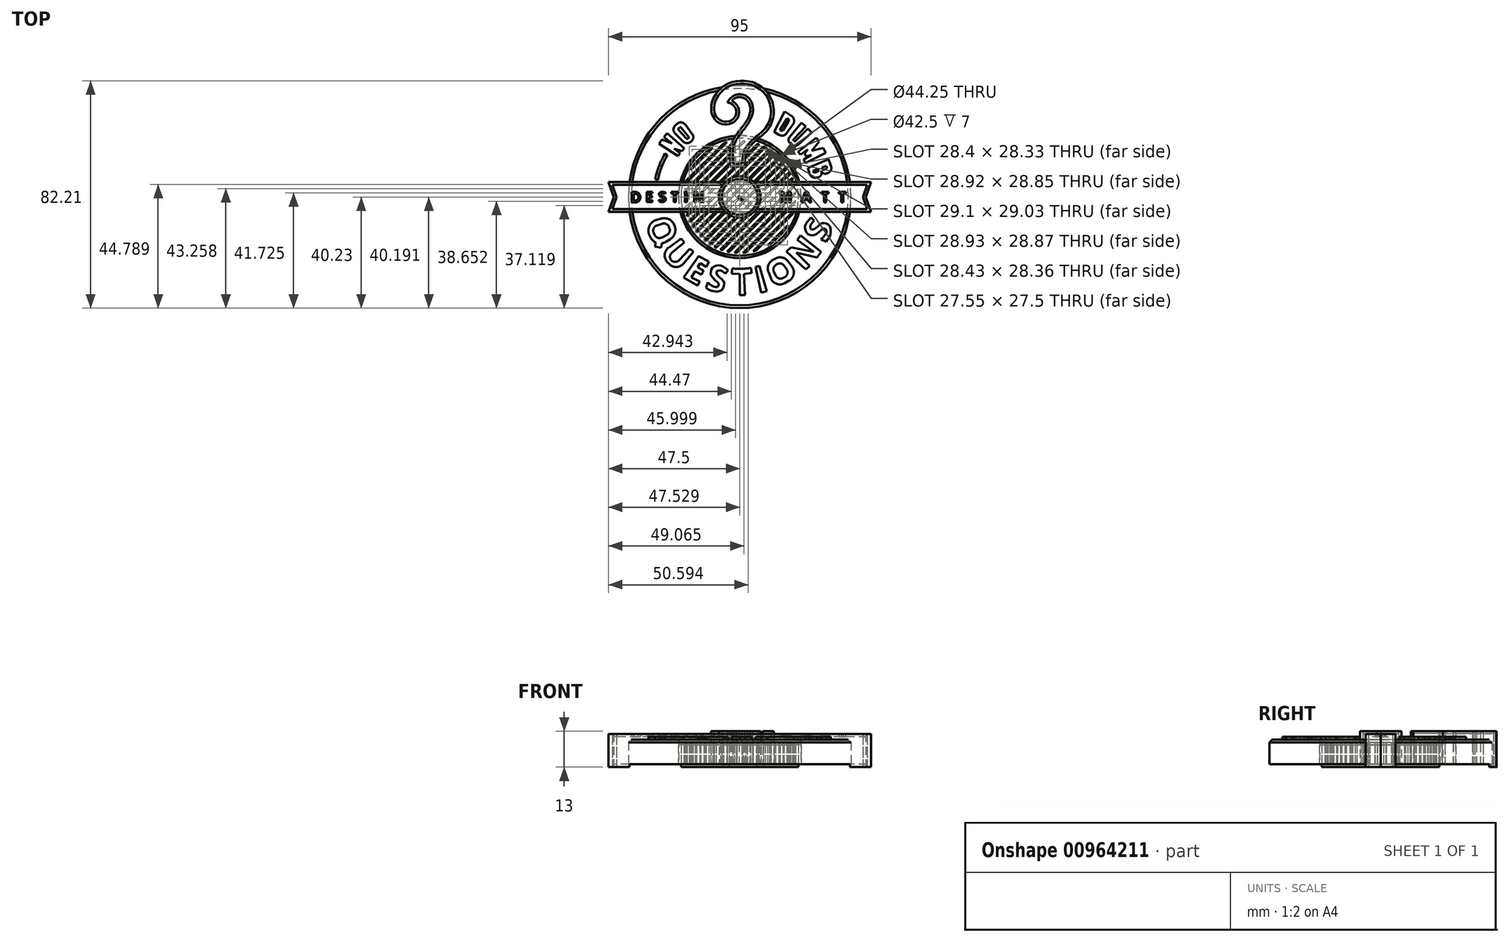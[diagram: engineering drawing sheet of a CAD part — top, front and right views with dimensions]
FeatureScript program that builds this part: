
annotation { "Feature Type Name" : "Feature", "Feature Type Description" : "" }
export const myFeature = defineFeature(function(context is Context, id is Id, definition is map)
    precondition{}
    {
        {
            var Q0;
            Q0=qCreatedBy(makeId("Top.planeOp"),FACE);
            cPlane(context, id + "F0", {"entities" : qUnion([Q0]), "cplaneType" : CPlaneType.OFFSET, "offset" : 11 * mm, "width" : 150 * mm, "height" : 150 * mm});
        }
        {
            var Q0;
            Q0=qCreatedBy(makeId("Top.planeOp"),FACE);
            var sketch = newSketch(context, id + "F1", { "sketchPlane" : qUnion([Q0])});
            skCircle(sketch, "E0", {"center": v(0, 0) * mm, "radius": 22.12 * mm});
            skCircle(sketch, "E1", {"center": v(0, 0) * mm, "radius": 40.23 * mm});
            skSolve(sketch);
        }
        {
            var Q0;
            Q0=qCreatedBy(makeId("Top.planeOp"),FACE);
            var sketch = newSketch(context, id + "F2", { "sketchPlane" : qUnion([Q0])});
            skCircle(sketch, "E2", {"center": v(0, 0) * mm, "radius": 22.25 * mm});
            skCircle(sketch, "E3.0", {"center": v(0, 0) * mm, "radius": 21.25 * mm});
            skCircle(sketch, "E4.0", {"center": v(0, 0) * mm, "radius": 20.25 * mm});
            skLineSegment(sketch, "E5", {"start": v(-14.52, -14.12) * mm, "end": v(14.16, 14.48) * mm});
            skLineSegment(sketch, "E6", {"start": v(-14.08, -14.55) * mm, "end": v(14.58, 14.05) * mm});
            skLineSegment(sketch, "E7.0.1.0", {"start": v(-15.97, -12.45) * mm, "end": v(12.5, 15.93) * mm});
            skLineSegment(sketch, "E7.0.2.0", {"start": v(-17.24, -10.62) * mm, "end": v(10.67, 17.21) * mm});
            skLineSegment(sketch, "E7.0.2.1", {"start": v(-16.9, -11.15) * mm, "end": v(11.18, 16.88) * mm});
            skLineSegment(sketch, "E7.1.7.0", {"start": v(-9.13, -18.07) * mm, "end": v(18.1, 9.08) * mm});
            skLineSegment(sketch, "E7.1.7.1", {"start": v(-8.54, -18.36) * mm, "end": v(18.37, 8.51) * mm});
            skLineSegment(sketch, "E7.1.8.0", {"start": v(-11.1, -16.93) * mm, "end": v(16.97, 11.05) * mm});
            skLineSegment(sketch, "E7.1.8.1", {"start": v(-10.57, -17.27) * mm, "end": v(17.3, 10.54) * mm});
            skLineSegment(sketch, "E7.1.9.0", {"start": v(-12.9, -15.61) * mm, "end": v(15.65, 12.85) * mm});
            skLineSegment(sketch, "E7.1.9.1", {"start": v(-12.4, -16) * mm, "end": v(16.02, 12.38) * mm});
            skLineSegment(sketch, "E8.trimOffspring", {"start": v(12.76, -15.72) * mm, "end": v(15.7, -12.8) * mm});
            skLineSegment(sketch, "E9.trimOffspring", {"start": v(10.02, -17.6) * mm, "end": v(17.57, -10.07) * mm});
            skLineSegment(sketch, "E10.trimOffspring", {"start": v(6.04, -19.33) * mm, "end": v(19.32, -6.07) * mm});
            skLineSegment(sketch, "E11.trimOffspring", {"start": v(4.83, -19.67) * mm, "end": v(19.65, -4.89) * mm});
            skLineSegment(sketch, "E12.trimOffspring", {"start": v(2.11, -20.14) * mm, "end": v(20.14, -2.15) * mm});
            skLineSegment(sketch, "E13.trimOffspring", {"start": v(1.16, -20.22) * mm, "end": v(20.21, -1.22) * mm});
            skLineSegment(sketch, "E14.trimOffspring", {"start": v(-1.9, -20.16) * mm, "end": v(20.17, 1.84) * mm});
            skLineSegment(sketch, "E15.trimOffspring", {"start": v(-1.08, -20.22) * mm, "end": v(20.22, 1.05) * mm});
            skLineSegment(sketch, "E16.trimOffspring", {"start": v(-3.85, -19.88) * mm, "end": v(19.89, 3.82) * mm});
            skLineSegment(sketch, "E17.trimOffspring", {"start": v(-4.58, -19.73) * mm, "end": v(19.74, 4.52) * mm});
            skLineSegment(sketch, "E18.trimOffspring", {"start": v(-6.32, -19.24) * mm, "end": v(19.25, 6.3) * mm});
            skLineSegment(sketch, "E19.trimOffspring", {"start": v(-6.98, -19.01) * mm, "end": v(19.03, 6.92) * mm});
            skLineSegment(sketch, "E20.trimOffspring", {"start": v(-15.58, -12.94) * mm, "end": v(12.97, 15.55) * mm});
            skLineSegment(sketch, "E21.trimOffspring", {"start": v(-18.05, -9.19) * mm, "end": v(9.22, 18.03) * mm});
            skLineSegment(sketch, "E22.trimOffspring", {"start": v(-18.33, -8.6) * mm, "end": v(8.66, 18.3) * mm});
            skLineSegment(sketch, "E23.trimOffspring", {"start": v(-19, -7.03) * mm, "end": v(7.06, 18.98) * mm});
            skLineSegment(sketch, "E24.trimOffspring", {"start": v(-19.22, -6.38) * mm, "end": v(6.44, 19.2) * mm});
            skLineSegment(sketch, "E25.trimOffspring", {"start": v(-19.71, -4.63) * mm, "end": v(4.7, 19.7) * mm});
            skLineSegment(sketch, "E26.trimOffspring", {"start": v(-19.87, -3.92) * mm, "end": v(3.98, 19.86) * mm});
            skLineSegment(sketch, "E27.trimOffspring", {"start": v(-20.15, -1.97) * mm, "end": v(2, 20.15) * mm});
            skLineSegment(sketch, "E28.trimOffspring", {"start": v(-20.22, -1.16) * mm, "end": v(1.22, 20.21) * mm});
            skLineSegment(sketch, "E29.trimOffspring", {"start": v(-20.22, 1.07) * mm, "end": v(-1.04, 20.22) * mm});
            skLineSegment(sketch, "E30.trimOffspring", {"start": v(-20.15, 2.01) * mm, "end": v(-1.95, 20.16) * mm});
            skLineSegment(sketch, "E31.trimOffspring", {"start": v(-19.7, 4.7) * mm, "end": v(-4.67, 19.7) * mm});
            skLineSegment(sketch, "E32.trimOffspring", {"start": v(-19.37, 5.9) * mm, "end": v(-5.83, 19.4) * mm});
            skLineSegment(sketch, "E33.trimOffspring", {"start": v(-17.74, 9.76) * mm, "end": v(-9.73, 17.76) * mm});
            skLineSegment(sketch, "E34.trimOffspring", {"start": v(-16.17, 12.2) * mm, "end": v(-12.15, 16.2) * mm});
            skSolve(sketch);
        }
        {
            var Q0;
            Q0=qCreatedBy(makeId("Top.planeOp"),FACE);
            var sketch = newSketch(context, id + "F3", { "sketchPlane" : qUnion([Q0])});
            skCircle(sketch, "E35", {"center": v(0, 0) * mm, "radius": 22.12 * mm});
            skSolve(sketch);
        }
        {
            var Q0;
            Q0=qCreatedBy(makeId("Top.planeOp"),FACE);
            cPlane(context, id + "F4", {"entities" : qUnion([Q0]), "cplaneType" : CPlaneType.OFFSET, "offset" : 10 * mm, "width" : 150 * mm, "height" : 150 * mm});
        }
        {
            var Q0;
            Q0=qCreatedBy(id+"F4.planeOp",FACE);
            var sketch = newSketch(context, id + "F5", { "sketchPlane" : qUnion([Q0])});
            skPoint(sketch, "E36.middle", {"position": v(0, 0) * mm});
            skArc(sketch, "E37", {"start": v(-17.48, 25.92) * mm, "mid": v(-14.44, 27.73) * mm, "end": v(-11.2, 29.19) * mm});
            skArc(sketch, "E38", {"start": v(-16.88, 25.03) * mm, "mid": v(-13.94, 26.78) * mm, "end": v(-10.82, 28.18) * mm});
            skLineSegment(sketch, "E39", {"start": v(0, 0) * mm, "end": v(-12.02, 31.32) * mm, "construction": true});
            skLineSegment(sketch, "E40", {"start": v(0, 0) * mm, "end": v(-17.92, 26.56) * mm, "construction": true});
            skLineSegment(sketch, "E41", {"start": v(0, 0) * mm, "end": v(-28.9, 16.69) * mm, "construction": true});
            skLineSegment(sketch, "E42", {"start": v(0, 0) * mm, "end": v(-31.67, 6.62) * mm, "construction": true});
            skArc(sketch, "E43", {"start": v(-26.19, 15.12) * mm, "mid": v(-28.25, 10.79) * mm, "end": v(-29.6, 6.18) * mm});
            skLineSegment(sketch, "E44", {"start": v(0, 0) * mm, "end": v(-36.69, 24.25) * mm, "construction": true});
            skLineSegment(sketch, "E45", {"start": v(0, 0) * mm, "end": v(-35.15, 25.88) * mm, "construction": true});
            skLineSegment(sketch, "E46", {"start": v(0, 0) * mm, "end": v(-34.07, 26.87) * mm, "construction": true});
            skLineSegment(sketch, "E47", {"start": v(0, 0) * mm, "end": v(-32.8, 28.77) * mm, "construction": true});
            skLineSegment(sketch, "E48", {"start": v(0, 0) * mm, "end": v(-26.52, 35.2) * mm, "construction": true});
            skLineSegment(sketch, "E49", {"start": v(-26.19, 15.12) * mm, "end": v(-27.08, 15.64) * mm});
            skLineSegment(sketch, "E50", {"start": v(-29.6, 6.18) * mm, "end": v(-30.61, 6.4) * mm});
            skLineSegment(sketch, "E51", {"start": v(-16.88, 25.03) * mm, "end": v(-17.48, 25.92) * mm});
            skLineSegment(sketch, "E52", {"start": v(-10.82, 28.18) * mm, "end": v(-11.2, 29.19) * mm});
            skArc(sketch, "E53", {"start": v(-26.73, 0) * mm, "mid": v(0, 26.73) * mm, "end": v(26.73, 0) * mm, "construction": true});
            skArc(sketch, "E54", {"start": v(-34.93, 0) * mm, "mid": v(0, 34.93) * mm, "end": v(34.93, 0) * mm, "construction": true});
            skLineSegment(sketch, "E55", {"start": v(0, 0) * mm, "end": v(-31.72, 31.17) * mm, "construction": true});
            skLineSegment(sketch, "E56", {"start": v(-22.3, 14.74) * mm, "end": v(-29.14, 19.26) * mm});
            skLineSegment(sketch, "E57", {"start": v(-21.52, 15.85) * mm, "end": v(-28.13, 20.71) * mm});
            skLineSegment(sketch, "E58", {"start": v(-20.98, 16.55) * mm, "end": v(-27.43, 21.64) * mm});
            skLineSegment(sketch, "E59", {"start": v(-20.1, 17.62) * mm, "end": v(-26.26, 23.04) * mm});
            skLineSegment(sketch, "E60", {"start": v(-28.13, 20.71) * mm, "end": v(-20.1, 17.62) * mm, "construction": true});
            skLineSegment(sketch, "E61", {"start": v(-20.98, 16.55) * mm, "end": v(-29.14, 19.26) * mm, "construction": true});
            skLineSegment(sketch, "E62", {"start": v(-19.73, 26.18) * mm, "end": v(-17.2, 22.83) * mm});
            skLineSegment(sketch, "E63", {"start": v(-23.38, 22.98) * mm, "end": v(-20.39, 20.03) * mm});
            skLineSegment(sketch, "E64", {"start": v(-23.3, 25.9) * mm, "end": v(-22.64, 26.48) * mm});
            skLineSegment(sketch, "E65", {"start": v(-17.67, 19.96) * mm, "end": v(-17.48, 20.12) * mm});
            skPoint(sketch, "E66.visualSharp", {"position": v(-21.02, 27.9) * mm});
            skArc(sketch, "E66.filletArc", {"start": v(-19.73, 26.18) * mm, "mid": v(-21.12, 26.97) * mm, "end": v(-22.64, 26.48) * mm});
            skPoint(sketch, "E67.visualSharp", {"position": v(-24.92, 24.49) * mm});
            skArc(sketch, "E67.filletArc", {"start": v(-23.3, 25.9) * mm, "mid": v(-23.98, 24.46) * mm, "end": v(-23.38, 22.98) * mm});
            skPoint(sketch, "E68.visualSharp", {"position": v(-16.08, 21.34) * mm});
            skArc(sketch, "E68.filletArc", {"start": v(-17.48, 20.12) * mm, "mid": v(-16.8, 21.42) * mm, "end": v(-17.2, 22.83) * mm});
            skPoint(sketch, "E69.visualSharp", {"position": v(-19.06, 18.73) * mm});
            skArc(sketch, "E69.filletArc", {"start": v(-20.39, 20.03) * mm, "mid": v(-19.04, 19.46) * mm, "end": v(-17.67, 19.96) * mm});
            skLineSegment(sketch, "E70", {"start": v(-20.98, 16.55) * mm, "end": v(-23.72, 17.46) * mm, "construction": true});
            skLineSegment(sketch, "E71", {"start": v(-20.98, 16.55) * mm, "end": v(-23.72, 17.46) * mm});
            skLineSegment(sketch, "E72", {"start": v(-28.13, 20.71) * mm, "end": v(-24.47, 19.3) * mm});
            skLineSegment(sketch, "E73", {"start": v(-29.14, 19.26) * mm, "end": v(-28.13, 20.71) * mm});
            skLineSegment(sketch, "E74", {"start": v(-27.43, 21.64) * mm, "end": v(-26.26, 23.04) * mm});
            skLineSegment(sketch, "E75", {"start": v(-20.98, 16.55) * mm, "end": v(-20.1, 17.62) * mm});
            skLineSegment(sketch, "E76", {"start": v(-22.3, 14.74) * mm, "end": v(-21.52, 15.85) * mm});
            skLineSegment(sketch, "E77", {"start": v(0, 0) * mm, "end": v(-29.4, 32.26) * mm, "construction": true});
            skLineSegment(sketch, "E78", {"start": v(0, 0) * mm, "end": v(-27.98, 33.07) * mm, "construction": true});
            skArc(sketch, "E79", {"start": v(28.2, 0) * mm, "mid": v(0, 28.2) * mm, "end": v(-28.2, 0) * mm, "construction": true});
            skArc(sketch, "E80", {"start": v(33.2, 0) * mm, "mid": v(0, 33.2) * mm, "end": v(-33.2, 0) * mm, "construction": true});
            skArc(sketch, "E81", {"start": v(30.07, 0) * mm, "mid": v(21.26, 21.26) * mm, "end": v(0, 30.07) * mm, "construction": true});
            skArc(sketch, "E82", {"start": v(31.59, 0) * mm, "mid": v(22.34, 22.34) * mm, "end": v(0, 31.59) * mm, "construction": true});
            skLineSegment(sketch, "E83", {"start": v(-19.26, 21.14) * mm, "end": v(-22.08, 24.23) * mm});
            skLineSegment(sketch, "E84", {"start": v(-22.04, 24.8) * mm, "end": v(-21.74, 25.07) * mm});
            skLineSegment(sketch, "E85", {"start": v(-21.17, 25.02) * mm, "end": v(-18.47, 21.83) * mm});
            skLineSegment(sketch, "E86", {"start": v(-18.51, 21.27) * mm, "end": v(-18.7, 21.1) * mm});
            skPoint(sketch, "E87.visualSharp", {"position": v(-22.36, 24.54) * mm});
            skArc(sketch, "E87.filletArc", {"start": v(-22.04, 24.8) * mm, "mid": v(-22.18, 24.53) * mm, "end": v(-22.08, 24.23) * mm});
            skPoint(sketch, "E88.visualSharp", {"position": v(-21.43, 25.33) * mm});
            skArc(sketch, "E88.filletArc", {"start": v(-21.17, 25.02) * mm, "mid": v(-21.45, 25.16) * mm, "end": v(-21.74, 25.07) * mm});
            skPoint(sketch, "E89.visualSharp", {"position": v(-18.22, 21.53) * mm});
            skArc(sketch, "E89.filletArc", {"start": v(-18.51, 21.27) * mm, "mid": v(-18.38, 21.54) * mm, "end": v(-18.47, 21.83) * mm});
            skPoint(sketch, "E90.visualSharp", {"position": v(-19, 20.85) * mm});
            skArc(sketch, "E90.filletArc", {"start": v(-19.26, 21.14) * mm, "mid": v(-18.98, 21) * mm, "end": v(-18.7, 21.1) * mm});
            skArc(sketch, "E91", {"start": v(-30.61, 6.4) * mm, "mid": v(-29.22, 11.16) * mm, "end": v(-27.08, 15.64) * mm});
            skLineSegment(sketch, "E92", {"start": v(0, 0) * mm, "end": v(19.18, 36.3) * mm, "construction": true});
            skLineSegment(sketch, "E93", {"start": v(0, 0) * mm, "end": v(21.24, 35.29) * mm, "construction": true});
            skLineSegment(sketch, "E94", {"start": v(0, 0) * mm, "end": v(22.48, 34.7) * mm, "construction": true});
            skLineSegment(sketch, "E95", {"start": v(0, 0) * mm, "end": v(24.33, 33.05) * mm, "construction": true});
            skLineSegment(sketch, "E96", {"start": v(0, 0) * mm, "end": v(26.82, 32.17) * mm, "construction": true});
            skLineSegment(sketch, "E97", {"start": v(0, 0) * mm, "end": v(28.64, 30.65) * mm, "construction": true});
            skLineSegment(sketch, "E98", {"start": v(0, 0) * mm, "end": v(30.98, 27.8) * mm, "construction": true});
            skLineSegment(sketch, "E99", {"start": v(0, 0) * mm, "end": v(29.35, 29.4) * mm, "construction": true});
            skLineSegment(sketch, "E100", {"start": v(0, 0) * mm, "end": v(32.72, 25.34) * mm, "construction": true});
            skLineSegment(sketch, "E101", {"start": v(0, 0) * mm, "end": v(38.58, 19.83) * mm, "construction": true});
            skLineSegment(sketch, "E102", {"start": v(0, 0) * mm, "end": v(39.4, 16.78) * mm, "construction": true});
            skLineSegment(sketch, "E103", {"start": v(0, 0) * mm, "end": v(40.92, 14.67) * mm, "construction": true});
            skLineSegment(sketch, "E104", {"start": v(0, 0) * mm, "end": v(41.16, 13.39) * mm, "construction": true});
            skLineSegment(sketch, "E105", {"start": v(0, 0) * mm, "end": v(42.33, 11.4) * mm, "construction": true});
            skLineSegment(sketch, "E106", {"start": v(0, 0) * mm, "end": v(41.86, 10.57) * mm, "construction": true});
            skLineSegment(sketch, "E107", {"start": v(0, 0) * mm, "end": v(34.36, 23.93) * mm, "construction": true});
            skLineSegment(sketch, "E108", {"start": v(0, 0) * mm, "end": v(37.3, 21.82) * mm, "construction": true});
            skLineSegment(sketch, "E109", {"start": v(0, 0) * mm, "end": v(35.65, 22.76) * mm, "construction": true});
            skLineSegment(sketch, "E110", {"start": v(0, 0) * mm, "end": v(34.66, 23.09) * mm, "construction": true});
            skLineSegment(sketch, "E111.MirrorCS", {"start": v(0, 0) * mm, "end": v(35.53, 21.73) * mm, "construction": true});
            skLineSegment(sketch, "E112", {"start": v(16.32, 30.89) * mm, "end": v(18.6, 29.46) * mm});
            skLineSegment(sketch, "E113", {"start": v(19.23, 26.12) * mm, "end": v(16.93, 23) * mm});
            skLineSegment(sketch, "E114", {"start": v(14.28, 22.46) * mm, "end": v(12.45, 23.57) * mm});
            skLineSegment(sketch, "E115", {"start": v(12.45, 23.57) * mm, "end": v(16.32, 30.89) * mm});
            skLineSegment(sketch, "E116", {"start": v(17.12, 28.44) * mm, "end": v(17.5, 28.22) * mm});
            skLineSegment(sketch, "E117", {"start": v(17.7, 27.32) * mm, "end": v(15.71, 24.25) * mm});
            skLineSegment(sketch, "E118", {"start": v(14.75, 24.05) * mm, "end": v(14.55, 24.17) * mm});
            skLineSegment(sketch, "E119", {"start": v(14.55, 24.17) * mm, "end": v(17.12, 28.44) * mm});
            skPoint(sketch, "E120.visualSharp", {"position": v(20.71, 28.13) * mm});
            skArc(sketch, "E120.filletArc", {"start": v(19.23, 26.12) * mm, "mid": v(19.64, 27.93) * mm, "end": v(18.6, 29.46) * mm});
            skPoint(sketch, "E121.visualSharp", {"position": v(15.85, 21.52) * mm});
            skArc(sketch, "E121.filletArc", {"start": v(14.28, 22.46) * mm, "mid": v(15.7, 22.21) * mm, "end": v(16.93, 23) * mm});
            skPoint(sketch, "E122.visualSharp", {"position": v(18.06, 27.88) * mm});
            skArc(sketch, "E122.filletArc", {"start": v(17.7, 27.32) * mm, "mid": v(17.79, 27.82) * mm, "end": v(17.5, 28.22) * mm});
            skPoint(sketch, "E123.visualSharp", {"position": v(15.33, 23.67) * mm});
            skArc(sketch, "E123.filletArc", {"start": v(14.75, 24.05) * mm, "mid": v(15.27, 23.95) * mm, "end": v(15.71, 24.25) * mm});
            skLineSegment(sketch, "E124", {"start": v(23.85, 25.52) * mm, "end": v(22.4, 26.88) * mm});
            skLineSegment(sketch, "E125", {"start": v(22.4, 26.88) * mm, "end": v(18, 21.6) * mm});
            skLineSegment(sketch, "E126", {"start": v(18.12, 19.56) * mm, "end": v(18.89, 18.82) * mm});
            skLineSegment(sketch, "E127", {"start": v(20.93, 18.78) * mm, "end": v(26, 23.33) * mm});
            skLineSegment(sketch, "E128", {"start": v(26, 23.33) * mm, "end": v(24.68, 24.72) * mm});
            skLineSegment(sketch, "E129", {"start": v(24.68, 24.72) * mm, "end": v(20.2, 20.24) * mm});
            skLineSegment(sketch, "E130", {"start": v(19.64, 20.24) * mm, "end": v(19.54, 20.34) * mm});
            skLineSegment(sketch, "E131", {"start": v(19.53, 20.9) * mm, "end": v(23.85, 25.52) * mm});
            skPoint(sketch, "E132.visualSharp", {"position": v(19.9, 17.85) * mm});
            skArc(sketch, "E132.filletArc", {"start": v(18.89, 18.82) * mm, "mid": v(19.9, 18.4) * mm, "end": v(20.93, 18.78) * mm});
            skPoint(sketch, "E133.visualSharp", {"position": v(17.11, 20.53) * mm});
            skArc(sketch, "E133.filletArc", {"start": v(18, 21.6) * mm, "mid": v(17.66, 20.56) * mm, "end": v(18.12, 19.56) * mm});
            skPoint(sketch, "E134.visualSharp", {"position": v(19.26, 20.62) * mm});
            skArc(sketch, "E134.filletArc", {"start": v(19.53, 20.9) * mm, "mid": v(19.42, 20.62) * mm, "end": v(19.54, 20.34) * mm});
            skPoint(sketch, "E135.visualSharp", {"position": v(19.92, 19.96) * mm});
            skArc(sketch, "E135.filletArc", {"start": v(19.64, 20.24) * mm, "mid": v(19.92, 20.12) * mm, "end": v(20.2, 20.24) * mm});
            skArc(sketch, "E136", {"start": v(30.94, 0) * mm, "mid": v(21.88, 21.88) * mm, "end": v(0, 30.94) * mm, "construction": true});
            skLineSegment(sketch, "E137", {"start": v(24.59, 10.47) * mm, "end": v(25.32, 8.3) * mm});
            skLineSegment(sketch, "E138", {"start": v(27.7, 7) * mm, "end": v(28.52, 7.2) * mm});
            skLineSegment(sketch, "E139", {"start": v(31.32, 8.43) * mm, "end": v(31.66, 8.52) * mm});
            skLineSegment(sketch, "E140", {"start": v(33.03, 11.1) * mm, "end": v(32.14, 13.7) * mm});
            skLineSegment(sketch, "E141", {"start": v(32.14, 13.7) * mm, "end": v(24.59, 10.47) * mm});
            skLineSegment(sketch, "E142", {"start": v(0, 0) * mm, "end": v(41.39, 12.16) * mm, "construction": true});
            skLineSegment(sketch, "E143", {"start": v(29.69, 8.72) * mm, "end": v(29.6, 9.05) * mm});
            skPoint(sketch, "E144.visualSharp", {"position": v(25.91, 6.54) * mm});
            skArc(sketch, "E144.filletArc", {"start": v(25.32, 8.3) * mm, "mid": v(26.26, 7.18) * mm, "end": v(27.7, 7) * mm});
            skPoint(sketch, "E145.visualSharp", {"position": v(30, 7.58) * mm});
            skArc(sketch, "E145.filletArc", {"start": v(28.52, 7.2) * mm, "mid": v(29.45, 7.9) * mm, "end": v(29.6, 9.05) * mm});
            skPoint(sketch, "E146.visualSharp", {"position": v(33.73, 9.08) * mm});
            skArc(sketch, "E146.filletArc", {"start": v(31.66, 8.52) * mm, "mid": v(32.9, 9.52) * mm, "end": v(33.03, 11.1) * mm});
            skLineSegment(sketch, "E147", {"start": v(29.48, 9.48) * mm, "end": v(29.69, 8.72) * mm});
            skPoint(sketch, "E148.visualSharp", {"position": v(29.87, 8.04) * mm});
            skArc(sketch, "E148.filletArc", {"start": v(29.48, 9.48) * mm, "mid": v(30.18, 8.58) * mm, "end": v(31.32, 8.43) * mm});
            skLineSegment(sketch, "E149", {"start": v(26.55, 9.52) * mm, "end": v(26.7, 9.1) * mm});
            skLineSegment(sketch, "E150", {"start": v(27.2, 8.84) * mm, "end": v(28.21, 9.18) * mm});
            skLineSegment(sketch, "E151", {"start": v(28.47, 9.68) * mm, "end": v(28.32, 10.15) * mm});
            skLineSegment(sketch, "E152", {"start": v(28.32, 10.15) * mm, "end": v(26.55, 9.52) * mm});
            skLineSegment(sketch, "E153", {"start": v(29.73, 10.66) * mm, "end": v(29.91, 10.14) * mm});
            skLineSegment(sketch, "E154", {"start": v(30.41, 9.9) * mm, "end": v(31.2, 10.14) * mm});
            skLineSegment(sketch, "E155", {"start": v(31.45, 10.65) * mm, "end": v(31.27, 11.21) * mm});
            skLineSegment(sketch, "E156", {"start": v(31.27, 11.21) * mm, "end": v(29.73, 10.66) * mm});
            skPoint(sketch, "E157.visualSharp", {"position": v(26.82, 8.72) * mm});
            skArc(sketch, "E157.filletArc", {"start": v(26.7, 9.1) * mm, "mid": v(26.89, 8.87) * mm, "end": v(27.2, 8.84) * mm});
            skPoint(sketch, "E158.visualSharp", {"position": v(28.6, 9.3) * mm});
            skArc(sketch, "E158.filletArc", {"start": v(28.21, 9.18) * mm, "mid": v(28.45, 9.37) * mm, "end": v(28.47, 9.68) * mm});
            skPoint(sketch, "E159.visualSharp", {"position": v(30.04, 9.77) * mm});
            skArc(sketch, "E159.filletArc", {"start": v(29.91, 10.14) * mm, "mid": v(30.11, 9.91) * mm, "end": v(30.41, 9.9) * mm});
            skPoint(sketch, "E160.visualSharp", {"position": v(31.57, 10.27) * mm});
            skArc(sketch, "E160.filletArc", {"start": v(31.2, 10.14) * mm, "mid": v(31.42, 10.34) * mm, "end": v(31.45, 10.65) * mm});
            skLineSegment(sketch, "E161", {"start": v(21.13, 16.36) * mm, "end": v(21.93, 15.28) * mm});
            skLineSegment(sketch, "E162", {"start": v(21.93, 15.28) * mm, "end": v(24.67, 17.19) * mm});
            skLineSegment(sketch, "E163", {"start": v(24.67, 17.19) * mm, "end": v(23.47, 15.63) * mm});
            skLineSegment(sketch, "E164", {"start": v(23.47, 15.63) * mm, "end": v(24.08, 14.72) * mm});
            skLineSegment(sketch, "E165", {"start": v(24.08, 14.72) * mm, "end": v(25.95, 15.19) * mm});
            skLineSegment(sketch, "E166", {"start": v(25.95, 15.19) * mm, "end": v(23.07, 13.5) * mm});
            skLineSegment(sketch, "E167", {"start": v(23.07, 13.5) * mm, "end": v(23.8, 12.24) * mm});
            skLineSegment(sketch, "E168", {"start": v(23.8, 12.24) * mm, "end": v(31.07, 15.97) * mm});
            skLineSegment(sketch, "E169", {"start": v(31.07, 15.97) * mm, "end": v(30.2, 17.67) * mm});
            skLineSegment(sketch, "E170", {"start": v(30.2, 17.67) * mm, "end": v(26.08, 16.65) * mm});
            skLineSegment(sketch, "E171", {"start": v(26.08, 16.65) * mm, "end": v(28.67, 19.97) * mm});
            skLineSegment(sketch, "E172", {"start": v(28.67, 19.97) * mm, "end": v(27.66, 21.42) * mm});
            skLineSegment(sketch, "E173", {"start": v(27.66, 21.42) * mm, "end": v(21.13, 16.36) * mm});
            skSolve(sketch);
        }
        {
            var Q0;
            Q0=qCreatedBy(id+"F4.planeOp",FACE);
            var sketch = newSketch(context, id + "F6", { "sketchPlane" : qUnion([Q0])});
            skArc(sketch, "E174", {"start": v(-26, 0) * mm, "mid": v(0, -26) * mm, "end": v(26, 0) * mm, "construction": true});
            skArc(sketch, "E175", {"start": v(-35.5, 0) * mm, "mid": v(0, -35.5) * mm, "end": v(35.5, 0) * mm, "construction": true});
            skLineSegment(sketch, "E176", {"start": v(0, 0) * mm, "end": v(-42.38, -11.68) * mm, "construction": true});
            skLineSegment(sketch, "E177", {"start": v(0, 0) * mm, "end": v(-42.12, -14.5) * mm, "construction": true});
            skLineSegment(sketch, "E178", {"start": v(0, 0) * mm, "end": v(-39.57, -20.63) * mm, "construction": true});
            skLineSegment(sketch, "E179", {"start": v(0, 0) * mm, "end": v(-38.55, -23.44) * mm, "construction": true});
            skLineSegment(sketch, "E180", {"start": v(0, 0) * mm, "end": v(-37.55, -24.34) * mm, "construction": true});
            skLineSegment(sketch, "E181", {"start": v(0, 0) * mm, "end": v(-36.48, -25.99) * mm, "construction": true});
            skLineSegment(sketch, "E182", {"start": v(0, 0) * mm, "end": v(-34.37, -28.21) * mm, "construction": true});
            skLineSegment(sketch, "E183", {"start": v(0, 0) * mm, "end": v(-30.39, -31.61) * mm, "construction": true});
            skLineSegment(sketch, "E184", {"start": v(0, 0) * mm, "end": v(-28.05, -33.25) * mm, "construction": true});
            skLineSegment(sketch, "E185", {"start": v(0, 0) * mm, "end": v(-24.41, -35.13) * mm, "construction": true});
            skLineSegment(sketch, "E186", {"start": v(0, 0) * mm, "end": v(-22.3, -37.12) * mm, "construction": true});
            skLineSegment(sketch, "E187", {"start": v(0, 0) * mm, "end": v(-18.67, -39.35) * mm, "construction": true});
            skLineSegment(sketch, "E188", {"start": v(0, 0) * mm, "end": v(-15.5, -40.87) * mm, "construction": true});
            skLineSegment(sketch, "E189", {"start": v(0, 0) * mm, "end": v(-12.8, -41.46) * mm, "construction": true});
            skLineSegment(sketch, "E190", {"start": v(0, 0) * mm, "end": v(-10.11, -42.04) * mm, "construction": true});
            skLineSegment(sketch, "E191", {"start": v(0, 0) * mm, "end": v(-7.42, -42.4) * mm, "construction": true});
            skLineSegment(sketch, "E192", {"start": v(0, 0) * mm, "end": v(-4.37, -42.4) * mm, "construction": true});
            skLineSegment(sketch, "E193", {"start": v(0, 0) * mm, "end": v(2.31, -42.28) * mm, "construction": true});
            skLineSegment(sketch, "E194", {"start": v(0, 0) * mm, "end": v(6.53, -41.7) * mm, "construction": true});
            skLineSegment(sketch, "E195", {"start": v(0, 0) * mm, "end": v(9.34, -41.7) * mm, "construction": true});
            skLineSegment(sketch, "E196", {"start": v(0, 0) * mm, "end": v(11.8, -41.1) * mm, "construction": true});
            skLineSegment(sketch, "E197", {"start": v(0, 0) * mm, "end": v(15.56, -40.64) * mm, "construction": true});
            skLineSegment(sketch, "E198", {"start": v(0, 0) * mm, "end": v(18.13, -39.58) * mm, "construction": true});
            skLineSegment(sketch, "E199", {"start": v(0, 0) * mm, "end": v(23.33, -36) * mm, "construction": true});
            skLineSegment(sketch, "E200", {"start": v(0, 0) * mm, "end": v(26.13, -34.86) * mm, "construction": true});
            skLineSegment(sketch, "E201", {"start": v(0, 0) * mm, "end": v(29.84, -32.78) * mm, "construction": true});
            skLineSegment(sketch, "E202", {"start": v(0, 0) * mm, "end": v(32.46, -31.96) * mm, "construction": true});
            skLineSegment(sketch, "E203", {"start": v(0, 0) * mm, "end": v(34.9, -26) * mm, "construction": true});
            skLineSegment(sketch, "E204", {"start": v(0, 0) * mm, "end": v(35.43, -23.91) * mm, "construction": true});
            skLineSegment(sketch, "E205", {"start": v(0, 0) * mm, "end": v(30.96, -29.01) * mm, "construction": true});
            skLineSegment(sketch, "E206", {"start": v(0, 0) * mm, "end": v(33.65, -26.3) * mm, "construction": true});
            skLineSegment(sketch, "E207", {"start": v(0, 0) * mm, "end": v(39.04, -20.72) * mm, "construction": true});
            skLineSegment(sketch, "E208", {"start": v(0, 0) * mm, "end": v(40.59, -18.27) * mm, "construction": true});
            skLineSegment(sketch, "E209", {"start": v(0, 0) * mm, "end": v(41.17, -15.7) * mm, "construction": true});
            skLineSegment(sketch, "E210", {"start": v(0, 0) * mm, "end": v(42.04, -12.99) * mm, "construction": true});
            skArc(sketch, "E211", {"start": v(-27.88, 0) * mm, "mid": v(0, -27.88) * mm, "end": v(27.88, 0) * mm, "construction": true});
            skArc(sketch, "E212", {"start": v(-33.84, 0) * mm, "mid": v(0, -33.84) * mm, "end": v(33.84, 0) * mm, "construction": true});
            skArc(sketch, "E213", {"start": v(-33.37, 0) * mm, "mid": v(0, -33.37) * mm, "end": v(33.37, 0) * mm, "construction": true});
            skArc(sketch, "E214", {"start": v(-31.33, 0) * mm, "mid": v(0, -31.33) * mm, "end": v(31.33, 0) * mm, "construction": true});
            skArc(sketch, "E215", {"start": v(-29.65, 0) * mm, "mid": v(0, -29.65) * mm, "end": v(29.65, 0) * mm, "construction": true});
            skArc(sketch, "E216", {"start": v(-35, 0) * mm, "mid": v(0, -35) * mm, "end": v(35, 0) * mm, "construction": true});
            skArc(sketch, "E217", {"start": v(-26.65, 0) * mm, "mid": v(0, -26.65) * mm, "end": v(26.65, 0) * mm, "construction": true});
            skArc(sketch, "E218", {"start": v(-34.6, 0) * mm, "mid": v(-24.47, -24.47) * mm, "end": v(0, -34.6) * mm, "construction": true});
            skArc(sketch, "E219", {"start": v(-32.7, 0) * mm, "mid": v(-23.13, -23.13) * mm, "end": v(0, -32.7) * mm, "construction": true});
            skLineSegment(sketch, "E220", {"start": v(0, 0) * mm, "end": v(-38.79, -22.77) * mm, "construction": true});
            skLineSegment(sketch, "E221", {"start": v(0, 0) * mm, "end": v(-39.38, -21.72) * mm, "construction": true});
            skLineSegment(sketch, "E222", {"start": v(0, 0) * mm, "end": v(-41.75, -17.7) * mm, "construction": true});
            skLineSegment(sketch, "E223", {"start": v(-28.4, -18.4) * mm, "end": v(-28.2, -16.56) * mm});
            skLineSegment(sketch, "E224", {"start": v(-28.4, -18.4) * mm, "end": v(-30.61, -17.97) * mm});
            skLineSegment(sketch, "E225", {"start": v(-32.68, -13.86) * mm, "end": v(-32.3, -14.62) * mm});
            skLineSegment(sketch, "E226", {"start": v(-26.66, -16.2) * mm, "end": v(-25.19, -15.32) * mm});
            skLineSegment(sketch, "E227", {"start": v(-23.6, -10.31) * mm, "end": v(-23.69, -10.1) * mm});
            skLineSegment(sketch, "E228", {"start": v(-28.42, -7.83) * mm, "end": v(-30.1, -8.3) * mm});
            skLineSegment(sketch, "E229", {"start": v(-32.82, -13.47) * mm, "end": v(-32.68, -13.86) * mm});
            skPoint(sketch, "E230.visualSharp", {"position": v(-25.07, -6.9) * mm});
            skArc(sketch, "E230.filletArc", {"start": v(-23.69, -10.1) * mm, "mid": v(-25.63, -8.08) * mm, "end": v(-28.42, -7.83) * mm});
            skPoint(sketch, "E231.visualSharp", {"position": v(-22.22, -13.5) * mm});
            skArc(sketch, "E231.filletArc", {"start": v(-25.19, -15.32) * mm, "mid": v(-23.46, -13.11) * mm, "end": v(-23.6, -10.31) * mm});
            skPoint(sketch, "E232.visualSharp", {"position": v(-30.33, -18.44) * mm});
            skArc(sketch, "E232.filletArc", {"start": v(-32.3, -14.62) * mm, "mid": v(-29.82, -16.64) * mm, "end": v(-26.66, -16.2) * mm});
            skPoint(sketch, "E233.visualSharp", {"position": v(-34.22, -9.43) * mm});
            skArc(sketch, "E233.filletArc", {"start": v(-30.1, -8.3) * mm, "mid": v(-32.58, -10.3) * mm, "end": v(-32.82, -13.47) * mm});
            skLineSegment(sketch, "E234", {"start": v(-30.61, -17.97) * mm, "end": v(-30.48, -16.39) * mm});
            skPoint(sketch, "E235.visualSharp", {"position": v(-27.58, -4.06) * mm});
            skLineSegment(sketch, "E236", {"start": v(-21.18, -15.08) * mm, "end": v(-25.68, -18.3) * mm});
            skLineSegment(sketch, "E237", {"start": v(-26.22, -23.52) * mm, "end": v(-25.58, -24.22) * mm});
            skLineSegment(sketch, "E238", {"start": v(-20.33, -24.1) * mm, "end": v(-16.76, -19.88) * mm});
            skLineSegment(sketch, "E239", {"start": v(-16.76, -19.88) * mm, "end": v(-18.06, -18.78) * mm});
            skLineSegment(sketch, "E240", {"start": v(-18.06, -18.78) * mm, "end": v(-21.98, -22.86) * mm});
            skLineSegment(sketch, "E241", {"start": v(-24.71, -23.03) * mm, "end": v(-24.89, -22.84) * mm});
            skLineSegment(sketch, "E242", {"start": v(-24.51, -20.12) * mm, "end": v(-20.1, -16.5) * mm});
            skLineSegment(sketch, "E243", {"start": v(-20.1, -16.5) * mm, "end": v(-21.18, -15.08) * mm});
            skPoint(sketch, "E244.visualSharp", {"position": v(-28.91, -20.6) * mm});
            skArc(sketch, "E244.filletArc", {"start": v(-25.68, -18.3) * mm, "mid": v(-27.13, -20.78) * mm, "end": v(-26.22, -23.52) * mm});
            skPoint(sketch, "E245.visualSharp", {"position": v(-22.89, -27.14) * mm});
            skArc(sketch, "E245.filletArc", {"start": v(-25.58, -24.22) * mm, "mid": v(-22.93, -25.35) * mm, "end": v(-20.33, -24.1) * mm});
            skPoint(sketch, "E246.visualSharp", {"position": v(-23.45, -24.4) * mm});
            skArc(sketch, "E246.filletArc", {"start": v(-24.89, -22.84) * mm, "mid": v(-23.44, -23.48) * mm, "end": v(-21.98, -22.86) * mm});
            skPoint(sketch, "E247.visualSharp", {"position": v(-26.15, -21.47) * mm});
            skArc(sketch, "E247.filletArc", {"start": v(-24.51, -20.12) * mm, "mid": v(-25.24, -21.53) * mm, "end": v(-24.71, -23.03) * mm});
            skLineSegment(sketch, "E248", {"start": v(-28.12, -9.67) * mm, "end": v(-29.96, -10.3) * mm});
            skLineSegment(sketch, "E249", {"start": v(-31.15, -12.99) * mm, "end": v(-30.86, -13.66) * mm});
            skLineSegment(sketch, "E250", {"start": v(-28.1, -14.64) * mm, "end": v(-26.37, -13.74) * mm});
            skLineSegment(sketch, "E251", {"start": v(-25.45, -11.18) * mm, "end": v(-25.63, -10.77) * mm});
            skPoint(sketch, "E252.visualSharp", {"position": v(-32, -11) * mm});
            skArc(sketch, "E252.filletArc", {"start": v(-29.96, -10.3) * mm, "mid": v(-31.14, -11.39) * mm, "end": v(-31.15, -12.99) * mm});
            skPoint(sketch, "E253.visualSharp", {"position": v(-30, -15.64) * mm});
            skArc(sketch, "E253.filletArc", {"start": v(-30.86, -13.66) * mm, "mid": v(-29.69, -14.76) * mm, "end": v(-28.1, -14.64) * mm});
            skPoint(sketch, "E254.visualSharp", {"position": v(-24.72, -12.89) * mm});
            skArc(sketch, "E254.filletArc", {"start": v(-26.37, -13.74) * mm, "mid": v(-25.4, -12.64) * mm, "end": v(-25.45, -11.18) * mm});
            skPoint(sketch, "E255.visualSharp", {"position": v(-26.36, -9.07) * mm});
            skArc(sketch, "E255.filletArc", {"start": v(-25.63, -10.77) * mm, "mid": v(-26.66, -9.73) * mm, "end": v(-28.12, -9.67) * mm});
            skLineSegment(sketch, "E256", {"start": v(-11.14, -23.5) * mm, "end": v(-14.84, -21.35) * mm});
            skLineSegment(sketch, "E257", {"start": v(-14.84, -21.35) * mm, "end": v(-20.26, -29.15) * mm});
            skLineSegment(sketch, "E258", {"start": v(-20.26, -29.15) * mm, "end": v(-15.22, -32.07) * mm});
            skLineSegment(sketch, "E259", {"start": v(-15.22, -32.07) * mm, "end": v(-14.5, -30.57) * mm});
            skLineSegment(sketch, "E260", {"start": v(-14.5, -30.57) * mm, "end": v(-17.5, -29.14) * mm});
            skLineSegment(sketch, "E261", {"start": v(-15.27, -25.42) * mm, "end": v(-14.36, -23.9) * mm});
            skLineSegment(sketch, "E262", {"start": v(-14.36, -23.9) * mm, "end": v(-12, -25.3) * mm});
            skLineSegment(sketch, "E263", {"start": v(-12, -25.3) * mm, "end": v(-11.14, -23.5) * mm});
            skLineSegment(sketch, "E264", {"start": v(0, 0) * mm, "end": v(-19.16, -39.14) * mm, "construction": true});
            skLineSegment(sketch, "E265", {"start": v(-17.5, -29.14) * mm, "end": v(-16.13, -26.85) * mm});
            skLineSegment(sketch, "E266", {"start": v(-16.13, -26.85) * mm, "end": v(-13.77, -28.13) * mm});
            skLineSegment(sketch, "E267", {"start": v(-13.77, -28.13) * mm, "end": v(-13.04, -26.63) * mm});
            skLineSegment(sketch, "E268", {"start": v(-13.04, -26.63) * mm, "end": v(-15.27, -25.42) * mm});
            skLineSegment(sketch, "E269", {"start": v(-2.67, -25.86) * mm, "end": v(-2.86, -27.73) * mm});
            skLineSegment(sketch, "E270", {"start": v(-2.86, -27.73) * mm, "end": v(0, -27.88) * mm});
            skLineSegment(sketch, "E271", {"start": v(0, -27.88) * mm, "end": v(0, -35.5) * mm});
            skLineSegment(sketch, "E272", {"start": v(0, -35.5) * mm, "end": v(1.94, -35.45) * mm});
            skLineSegment(sketch, "E273", {"start": v(1.94, -35.45) * mm, "end": v(1.52, -27.84) * mm});
            skLineSegment(sketch, "E274", {"start": v(1.52, -27.84) * mm, "end": v(4.31, -27.54) * mm});
            skLineSegment(sketch, "E275", {"start": v(4.31, -27.54) * mm, "end": v(4.02, -25.69) * mm});
            skLineSegment(sketch, "E276", {"start": v(5.69, -25.37) * mm, "end": v(7.76, -34.64) * mm});
            skLineSegment(sketch, "E277", {"start": v(7.76, -34.64) * mm, "end": v(9.8, -34.12) * mm});
            skLineSegment(sketch, "E278", {"start": v(9.8, -34.12) * mm, "end": v(7.18, -25) * mm});
            skLineSegment(sketch, "E279", {"start": v(7.18, -25) * mm, "end": v(5.69, -25.37) * mm});
            skArc(sketch, "E280", {"start": v(4.02, -25.69) * mm, "mid": v(0.68, -26) * mm, "end": v(-2.67, -25.86) * mm});
            skLineSegment(sketch, "E281", {"start": v(10.38, -27.13) * mm, "end": v(11.25, -29.4) * mm});
            skLineSegment(sketch, "E282", {"start": v(16.21, -31.2) * mm, "end": v(17.77, -30.35) * mm});
            skLineSegment(sketch, "E283", {"start": v(18.88, -25.18) * mm, "end": v(17.42, -23.24) * mm});
            skLineSegment(sketch, "E284", {"start": v(12.93, -22.27) * mm, "end": v(11.96, -22.81) * mm});
            skLineSegment(sketch, "E285", {"start": v(12.39, -27.04) * mm, "end": v(13, -28.38) * mm});
            skLineSegment(sketch, "E286", {"start": v(16.98, -26.2) * mm, "end": v(16.17, -24.95) * mm});
            skLineSegment(sketch, "E287", {"start": v(13.53, -24.29) * mm, "end": v(13.24, -24.45) * mm});
            skPoint(sketch, "E288.visualSharp", {"position": v(12.7, -33.15) * mm});
            skArc(sketch, "E288.filletArc", {"start": v(11.25, -29.4) * mm, "mid": v(13.32, -31.43) * mm, "end": v(16.21, -31.2) * mm});
            skPoint(sketch, "E289.visualSharp", {"position": v(21.3, -28.4) * mm});
            skArc(sketch, "E289.filletArc", {"start": v(17.77, -30.35) * mm, "mid": v(19.5, -28.02) * mm, "end": v(18.88, -25.18) * mm});
            skPoint(sketch, "E290.visualSharp", {"position": v(15.6, -20.8) * mm});
            skArc(sketch, "E290.filletArc", {"start": v(17.42, -23.24) * mm, "mid": v(15.36, -21.92) * mm, "end": v(12.93, -22.27) * mm});
            skPoint(sketch, "E291.visualSharp", {"position": v(9.3, -24.28) * mm});
            skArc(sketch, "E291.filletArc", {"start": v(11.96, -22.81) * mm, "mid": v(10.36, -24.67) * mm, "end": v(10.38, -27.13) * mm});
            skPoint(sketch, "E292.visualSharp", {"position": v(15.16, -23.4) * mm});
            skArc(sketch, "E292.filletArc", {"start": v(16.17, -24.95) * mm, "mid": v(14.98, -24.1) * mm, "end": v(13.53, -24.29) * mm});
            skPoint(sketch, "E293.visualSharp", {"position": v(11.61, -25.34) * mm});
            skArc(sketch, "E293.filletArc", {"start": v(13.24, -24.45) * mm, "mid": v(12.3, -25.57) * mm, "end": v(12.39, -27.04) * mm});
            skLineSegment(sketch, "E294", {"start": v(17.5, -19.23) * mm, "end": v(23.9, -26.25) * mm});
            skLineSegment(sketch, "E295", {"start": v(23.9, -26.25) * mm, "end": v(25.33, -24.95) * mm});
            skLineSegment(sketch, "E296", {"start": v(25.33, -24.95) * mm, "end": v(19.86, -19.56) * mm});
            skLineSegment(sketch, "E297", {"start": v(27.97, -21.86) * mm, "end": v(29.42, -19.86) * mm});
            skLineSegment(sketch, "E298", {"start": v(29.42, -19.86) * mm, "end": v(21.97, -13.9) * mm});
            skLineSegment(sketch, "E299", {"start": v(21.97, -13.9) * mm, "end": v(20.85, -15.53) * mm});
            skLineSegment(sketch, "E300", {"start": v(20.85, -15.53) * mm, "end": v(26.76, -19.93) * mm});
            skLineSegment(sketch, "E301", {"start": v(26.76, -19.93) * mm, "end": v(18.53, -18.24) * mm});
            skLineSegment(sketch, "E302", {"start": v(18.53, -18.24) * mm, "end": v(16.86, -19.8) * mm});
            skLineSegment(sketch, "E303", {"start": v(0, 0) * mm, "end": v(29, -34.05) * mm, "construction": true});
            skLineSegment(sketch, "E304", {"start": v(0, 0) * mm, "end": v(37.93, -24.02) * mm, "construction": true});
            skLineSegment(sketch, "E305", {"start": v(23.9, -26.25) * mm, "end": v(16.86, -19.8) * mm});
            skLineSegment(sketch, "E306", {"start": v(15.78, -29.3) * mm, "end": v(16.26, -29.04) * mm});
            skPoint(sketch, "E307.visualSharp", {"position": v(18.15, -28) * mm});
            skArc(sketch, "E307.filletArc", {"start": v(16.26, -29.04) * mm, "mid": v(17.24, -27.77) * mm, "end": v(16.98, -26.2) * mm});
            skPoint(sketch, "E308.visualSharp", {"position": v(13.9, -30.34) * mm});
            skArc(sketch, "E308.filletArc", {"start": v(13, -28.38) * mm, "mid": v(14.2, -29.45) * mm, "end": v(15.78, -29.3) * mm});
            skLineSegment(sketch, "E309", {"start": v(19.86, -19.56) * mm, "end": v(21.13, -20.8) * mm});
            skLineSegment(sketch, "E310", {"start": v(27.97, -21.86) * mm, "end": v(20.5, -20.18) * mm});
            skFitSpline(sketch, "E311", {"points": [v(-4.16, -26.46) * mm, v(-6.76, -24.88) * mm, v(-8.38, -24.8) * mm, v(-10, -25.75) * mm, v(-10.5, -27.12) * mm, v(-10.2, -28.65) * mm, v(-7.96, -30.93) * mm, v(-7.55, -31.71) * mm, v(-7.84, -32.33) * mm, v(-8.5, -32.59) * mm, v(-9.8, -32.24) * mm, v(-11.58, -30.98) * mm], "startDerivative": vector(-21.8, 15.36) * mm, "endDerivative": vector(-16.83, 13.47) * mm});
            skLineSegment(sketch, "E312", {"start": v(-11.58, -30.98) * mm, "end": v(-12.14, -32.89) * mm});
            skLineSegment(sketch, "E313", {"start": v(-4.16, -26.46) * mm, "end": v(-5.16, -27.7) * mm});
            skFitSpline(sketch, "E314", {"points": [v(-12.14, -32.89) * mm, v(-10.8, -33.69) * mm, v(-9.17, -34.13) * mm, v(-7.99, -34.26) * mm, v(-6.3, -33.43) * mm, v(-5.62, -31.61) * mm, v(-6, -30.24) * mm, v(-8.24, -28.1) * mm, v(-8.4, -27.2) * mm, v(-8.18, -26.8) * mm, v(-7.19, -26.6) * mm, v(-6.33, -26.91) * mm, v(-5.16, -27.7) * mm], "startDerivative": vector(14.29, -10.06) * mm, "endDerivative": vector(14.44, -10.42) * mm});
            skFitSpline(sketch, "E315", {"points": [v(25.83, -7.43) * mm, v(23.93, -9.82) * mm, v(23.65, -11.4) * mm, v(24.4, -13.13) * mm, v(25.7, -13.8) * mm, v(27.25, -13.7) * mm, v(29.79, -11.76) * mm, v(30.62, -11.45) * mm, v(31.2, -11.81) * mm, v(31.37, -12.5) * mm, v(30.86, -13.74) * mm, v(29.39, -15.35) * mm], "startDerivative": vector(-17.95, -19.73) * mm, "endDerivative": vector(-15.45, -15.03) * mm});
            skLineSegment(sketch, "E316", {"start": v(29.39, -15.35) * mm, "end": v(31.21, -16.15) * mm});
            skLineSegment(sketch, "E317", {"start": v(25.83, -7.43) * mm, "end": v(26.93, -8.57) * mm});
            skFitSpline(sketch, "E318", {"points": [v(31.21, -16.15) * mm, v(32.17, -14.92) * mm, v(32.82, -13.36) * mm, v(32.48, -10.42) * mm, v(30.76, -9.52) * mm, v(29.35, -9.73) * mm, v(26.94, -11.69) * mm, v(26.04, -11.73) * mm, v(25.6, -11.36) * mm, v(25.58, -10.45) * mm, v(26, -9.64) * mm, v(26.93, -8.57) * mm], "startDerivative": vector(11.75, 12.93) * mm, "endDerivative": vector(12.13, 13.03) * mm});
            skSolve(sketch);
        }
        {
            var Q0;
            Q0=qCreatedBy(makeId("Top.planeOp"),FACE);
            var sketch = newSketch(context, id + "F7", { "sketchPlane" : qUnion([Q0])});
            skLineSegment(sketch, "E319.bottom", {"start": v(47.5, -5.4) * mm, "end": v(-47.5, -5.4) * mm});
            skLineSegment(sketch, "E319.top", {"start": v(47.5, 5.4) * mm, "end": v(-47.5, 5.4) * mm});
            skLineSegment(sketch, "E320", {"start": v(45.59, 0) * mm, "end": v(47.5, -5.4) * mm});
            skLineSegment(sketch, "E321", {"start": v(45.59, 0) * mm, "end": v(47.5, 5.4) * mm});
            skLineSegment(sketch, "E322", {"start": v(-45.59, 0) * mm, "end": v(-47.5, 5.4) * mm});
            skLineSegment(sketch, "E323", {"start": v(-45.59, 0) * mm, "end": v(-47.5, -5.4) * mm});
            skLineSegment(sketch, "E324.0", {"start": v(44.53, 0) * mm, "end": v(46.09, -4.4) * mm});
            skLineSegment(sketch, "E324.1", {"start": v(46.09, -4.4) * mm, "end": v(-46.09, -4.4) * mm});
            skLineSegment(sketch, "E324.2", {"start": v(-44.53, 0) * mm, "end": v(-46.09, -4.4) * mm});
            skLineSegment(sketch, "E325.0", {"start": v(44.53, 0) * mm, "end": v(46.09, 4.4) * mm});
            skLineSegment(sketch, "E325.1", {"start": v(46.09, 4.4) * mm, "end": v(-46.09, 4.4) * mm});
            skLineSegment(sketch, "E325.2", {"start": v(-44.53, 0) * mm, "end": v(-46.09, 4.4) * mm});
            skSolve(sketch);
        }
        {
            var Q0;
            Q0=qCreatedBy(makeId("Top.planeOp"),FACE);
            var sketch = newSketch(context, id + "F8", { "sketchPlane" : qUnion([Q0])});
            skLineSegment(sketch, "E326", {"start": v(-2.47, 11.97) * mm, "end": v(0.8, 11.97) * mm});
            skPoint(sketch, "E327", {"position": v(-0.99, 21.02) * mm});
            skPoint(sketch, "E328", {"position": v(7.72, 23.27) * mm});
            skFitSpline(sketch, "E329", {"points": [v(-0.99, 21.02) * mm, v(-2.47, 11.97) * mm], "startDerivative": vector(-6.2, -10.24) * mm, "endDerivative": vector(-0.54, -10.85) * mm});
            skFitSpline(sketch, "E330", {"points": [v(7.72, 23.27) * mm, v(3.22, 19.19) * mm, v(1.4, 16) * mm, v(0.8, 11.97) * mm], "startDerivative": vector(-13.35, -10.58) * mm, "endDerivative": vector(-1.17, -13.33) * mm});
            skArc(sketch, "E331", {"start": v(-4.02, 27.36) * mm, "mid": v(-1.25, 30.9) * mm, "end": v(-4.4, 34.1) * mm});
            skArc(sketch, "E332", {"start": v(7.72, 23.27) * mm, "mid": v(10.95, 33.7) * mm, "end": v(2.71, 40.87) * mm});
            skFitSpline(sketch, "E333", {"points": [v(2.71, 40.87) * mm, v(-2.39, 40.55) * mm, v(-6.82, 37.85) * mm, v(-9.18, 33.34) * mm, v(-9.1, 30.4) * mm, v(-8.07, 28.49) * mm, v(-6.19, 27.36) * mm, v(-4.02, 27.36) * mm], "startDerivative": vector(-30.15, 2.21) * mm, "endDerivative": vector(14.25, 2.75) * mm});
            skArc(sketch, "E334", {"start": v(4.55, 33.47) * mm, "mid": v(0.31, 37.1) * mm, "end": v(-4.4, 34.1) * mm});
            skFitSpline(sketch, "E335", {"points": [v(4.55, 33.47) * mm, v(4.73, 30.53) * mm, v(3.67, 27.58) * mm, v(1.96, 25.06) * mm, v(-0.99, 21.02) * mm], "startDerivative": vector(3.23, -12.35) * mm, "endDerivative": vector(-9.9, -15.67) * mm});
            skCircle(sketch, "E336", {"center": v(0, 0) * mm, "radius": 7.5 * mm});
            skCircle(sketch, "E337.0", {"center": v(0, 0) * mm, "radius": 6.5 * mm});
            skFitSpline(sketch, "E338.0", {"points": [v(8.34, 22.49) * mm, v(7.8, 22.05) * mm, v(6.7, 21.17) * mm, v(5.23, 19.87) * mm, v(4, 18.62) * mm, v(3.12, 17.47) * mm, v(2.63, 16.52) * mm, v(2.34, 15.7) * mm, v(2.18, 15.03) * mm, v(2.05, 14.3) * mm, v(1.92, 13.27) * mm, v(1.85, 12.44) * mm, v(1.8, 11.89) * mm]});
            skLineSegment(sketch, "E338.1", {"start": v(-3.47, 10.97) * mm, "end": v(1.78, 10.97) * mm});
            skArc(sketch, "E338.2", {"start": v(8.35, 22.5) * mm, "mid": v(11.91, 33.99) * mm, "end": v(2.82, 41.86) * mm});
            skFitSpline(sketch, "E338.3", {"points": [v(-1.84, 21.54) * mm, v(-2.4, 20.63) * mm, v(-2.96, 19.36) * mm, v(-3.33, 17.77) * mm, v(-3.5, 16.25) * mm, v(-3.45, 14.44) * mm, v(-3.43, 12.89) * mm, v(-3.47, 12.02) * mm]});
            skFitSpline(sketch, "E338.4", {"points": [v(2.79, 41.86) * mm, v(2.14, 41.91) * mm, v(0.85, 41.98) * mm, v(-0.78, 41.89) * mm, v(-2.08, 41.67) * mm, v(-3.37, 41.33) * mm, v(-4.94, 40.66) * mm, v(-6.38, 39.68) * mm, v(-7.4, 38.72) * mm, v(-8.34, 37.64) * mm, v(-9.28, 36.14) * mm, v(-9.92, 34.59) * mm, v(-10.22, 33.37) * mm, v(-10.33, 32.5) * mm, v(-10.33, 31.66) * mm, v(-10.24, 30.88) * mm, v(-10.08, 30.15) * mm, v(-9.84, 29.47) * mm, v(-9.53, 28.81) * mm, v(-9.14, 28.2) * mm, v(-8.67, 27.65) * mm, v(-8.1, 27.15) * mm, v(-7.45, 26.74) * mm, v(-6.84, 26.49) * mm, v(-6.3, 26.35) * mm, v(-5.77, 26.27) * mm, v(-5.12, 26.24) * mm, v(-4.42, 26.28) * mm, v(-4.01, 26.34) * mm, v(-3.84, 26.37) * mm]});
            skArc(sketch, "E338.5", {"start": v(-3.84, 26.37) * mm, "mid": v(-0.27, 30.2) * mm, "end": v(-2.88, 34.74) * mm});
            skArc(sketch, "E338.6", {"start": v(3.58, 33.23) * mm, "mid": v(0.82, 36) * mm, "end": v(-2.88, 34.74) * mm});
            skFitSpline(sketch, "E338.7", {"points": [v(3.59, 33.22) * mm, v(3.7, 32.77) * mm, v(3.81, 32.08) * mm, v(3.8, 31.15) * mm, v(3.72, 30.47) * mm, v(3.53, 29.76) * mm, v(3.28, 29.05) * mm, v(2.96, 28.36) * mm, v(2.6, 27.71) * mm, v(2.22, 27.1) * mm, v(1.78, 26.48) * mm, v(1.3, 25.83) * mm, v(0.73, 25.11) * mm, v(0.12, 24.32) * mm, v(-0.74, 23.19) * mm, v(-1.4, 22.24) * mm, v(-1.83, 21.56) * mm]});
            skLineSegment(sketch, "E339", {"start": v(-3.47, 12.02) * mm, "end": v(-3.47, 10.97) * mm});
            skLineSegment(sketch, "E340", {"start": v(1.8, 11.89) * mm, "end": v(1.78, 10.97) * mm});
            skLineSegment(sketch, "E341", {"start": v(-1.83, 21.56) * mm, "end": v(-1.84, 21.54) * mm});
            skLineSegment(sketch, "E342", {"start": v(3.58, 33.23) * mm, "end": v(3.59, 33.22) * mm});
            skLineSegment(sketch, "E343", {"start": v(2.79, 41.86) * mm, "end": v(2.82, 41.86) * mm});
            skLineSegment(sketch, "E344", {"start": v(8.34, 22.49) * mm, "end": v(8.35, 22.5) * mm});
            skSolve(sketch);
        }
        {
            var Q0;
            Q0=qCreatedBy(id+"F0.planeOp",FACE);
            var sketch = newSketch(context, id + "F9", { "sketchPlane" : qUnion([Q0])});
            skLineSegment(sketch, "E345.bottom", {"start": v(-39.06, 1.8) * mm, "end": v(-37.74, 1.8) * mm});
            skLineSegment(sketch, "E345.top", {"start": v(-39.06, -2) * mm, "end": v(-37.74, -2) * mm});
            skLineSegment(sketch, "E345.left", {"start": v(-39.06, 1.8) * mm, "end": v(-39.06, -2) * mm});
            skLineSegment(sketch, "E345.right", {"start": v(-35.94, 0) * mm, "end": v(-35.94, -0.2) * mm});
            skPoint(sketch, "E346.visualSharp", {"position": v(-35.94, 1.8) * mm});
            skArc(sketch, "E346.filletArc", {"start": v(-35.94, 0) * mm, "mid": v(-36.47, 1.27) * mm, "end": v(-37.74, 1.8) * mm});
            skPoint(sketch, "E347.visualSharp", {"position": v(-35.94, -2) * mm});
            skArc(sketch, "E347.filletArc", {"start": v(-37.74, -2) * mm, "mid": v(-36.47, -1.46) * mm, "end": v(-35.94, -0.2) * mm});
            skLineSegment(sketch, "E348", {"start": v(-33.66, 1.9) * mm, "end": v(-33.66, -1.9) * mm});
            skPoint(sketch, "E348.endSnap0", {"position": v(-38.4, -2) * mm});
            skLineSegment(sketch, "E349", {"start": v(-33.66, -1.9) * mm, "end": v(-31.56, -1.9) * mm});
            skLineSegment(sketch, "E350", {"start": v(-31.56, -1.9) * mm, "end": v(-31.56, -1.26) * mm});
            skLineSegment(sketch, "E351", {"start": v(-31.56, -1.26) * mm, "end": v(-32.86, -1.26) * mm});
            skLineSegment(sketch, "E352", {"start": v(-32.86, -1.26) * mm, "end": v(-32.86, -0.2) * mm});
            skLineSegment(sketch, "E353", {"start": v(-32.86, -0.2) * mm, "end": v(-31.7, -0.2) * mm});
            skLineSegment(sketch, "E354", {"start": v(-31.7, -0.2) * mm, "end": v(-31.7, 0.44) * mm});
            skLineSegment(sketch, "E355", {"start": v(-31.7, 0.44) * mm, "end": v(-32.86, 0.44) * mm});
            skLineSegment(sketch, "E356", {"start": v(-32.86, 0.44) * mm, "end": v(-32.86, 1.27) * mm});
            skLineSegment(sketch, "E357", {"start": v(-32.86, 1.27) * mm, "end": v(-31.56, 1.27) * mm});
            skLineSegment(sketch, "E358", {"start": v(-31.56, 1.27) * mm, "end": v(-31.56, 1.9) * mm});
            skLineSegment(sketch, "E359", {"start": v(-31.56, 1.9) * mm, "end": v(-33.66, 1.9) * mm});
            skLineSegment(sketch, "E360.0", {"start": v(-38.36, 1.1) * mm, "end": v(-38.36, -1.3) * mm});
            skArc(sketch, "E360.1", {"start": v(-36.64, 0) * mm, "mid": v(-36.97, 0.78) * mm, "end": v(-37.74, 1.1) * mm});
            skLineSegment(sketch, "E360.2", {"start": v(-36.64, 0) * mm, "end": v(-36.64, -0.2) * mm});
            skLineSegment(sketch, "E360.3", {"start": v(-38.36, 1.1) * mm, "end": v(-37.74, 1.1) * mm});
            skArc(sketch, "E360.4", {"start": v(-37.74, -1.3) * mm, "mid": v(-36.97, -0.97) * mm, "end": v(-36.64, -0.2) * mm});
            skLineSegment(sketch, "E360.5", {"start": v(-38.36, -1.3) * mm, "end": v(-37.74, -1.3) * mm});
            skLineSegment(sketch, "E361", {"start": v(-51.1, 1.8) * mm, "end": v(49.4, 1.8) * mm, "construction": true});
            skLineSegment(sketch, "E362", {"start": v(-51.1, -2) * mm, "end": v(49.4, -1.9) * mm, "construction": true});
            skFitSpline(sketch, "E363", {"points": [v(-29.19, -0.94) * mm, v(-28.45, -1.2) * mm, v(-27.84, -1.2) * mm, v(-27.53, -0.93) * mm, v(-27.67, -0.48) * mm, v(-28.2, -0.17) * mm, v(-28.88, 0.28) * mm, v(-29.16, 0.93) * mm, v(-28.97, 1.5) * mm, v(-28.45, 1.8) * mm, v(-27.85, 1.85) * mm, v(-26.84, 1.66) * mm], "startDerivative": vector(6.84, -3.18) * mm, "endDerivative": vector(11.6, -2.74) * mm});
            skLineSegment(sketch, "E364", {"start": v(-26.84, 1.66) * mm, "end": v(-27.05, 1.08) * mm});
            skFitSpline(sketch, "E365", {"points": [v(-27.05, 1.08) * mm, v(-27.66, 1.27) * mm, v(-28.17, 1.26) * mm, v(-28.39, 1.02) * mm, v(-28.3, 0.74) * mm, v(-27.84, 0.34) * mm, v(-27.2, 0) * mm, v(-26.92, -0.24) * mm, v(-26.79, -0.67) * mm, v(-26.88, -1.21) * mm, v(-27.24, -1.6) * mm, v(-27.64, -1.8) * mm, v(-28.12, -1.85) * mm, v(-28.64, -1.79) * mm, v(-29.19, -1.61) * mm], "startDerivative": vector(-7.4, 2.87) * mm, "endDerivative": vector(-7.1, 2.63) * mm});
            skLineSegment(sketch, "E366", {"start": v(-29.19, -0.94) * mm, "end": v(-29.19, -1.61) * mm});
            skLineSegment(sketch, "E367", {"start": v(-24.75, 1.88) * mm, "end": v(-24.75, 1.27) * mm});
            skLineSegment(sketch, "E368", {"start": v(-24.75, 1.27) * mm, "end": v(-23.84, 1.27) * mm});
            skLineSegment(sketch, "E369", {"start": v(-23.84, 1.27) * mm, "end": v(-23.84, -1.89) * mm});
            skLineSegment(sketch, "E370", {"start": v(-23.84, -1.89) * mm, "end": v(-23.13, -1.89) * mm});
            skLineSegment(sketch, "E371", {"start": v(-23.13, -1.89) * mm, "end": v(-23.13, 1.27) * mm});
            skLineSegment(sketch, "E372", {"start": v(-23.13, 1.27) * mm, "end": v(-22.21, 1.27) * mm});
            skLineSegment(sketch, "E373", {"start": v(-22.21, 1.27) * mm, "end": v(-22.21, 1.88) * mm});
            skLineSegment(sketch, "E374", {"start": v(-22.21, 1.88) * mm, "end": v(-24.75, 1.88) * mm});
            skLineSegment(sketch, "E375.bottom", {"start": v(-19.81, 1.88) * mm, "end": v(-19.1, 1.88) * mm});
            skLineSegment(sketch, "E375.top", {"start": v(-19.81, -1.88) * mm, "end": v(-19.1, -1.88) * mm});
            skLineSegment(sketch, "E375.left", {"start": v(-19.81, 1.88) * mm, "end": v(-19.81, -1.88) * mm});
            skLineSegment(sketch, "E375.right", {"start": v(-19.1, 1.88) * mm, "end": v(-19.1, -1.88) * mm});
            skLineSegment(sketch, "E376.bottom", {"start": v(-16.5, 1.88) * mm, "end": v(-15.8, 1.88) * mm});
            skLineSegment(sketch, "E376.top", {"start": v(-16.5, -1.88) * mm, "end": v(-15.8, -1.88) * mm});
            skLineSegment(sketch, "E376.left", {"start": v(-16.5, 1.88) * mm, "end": v(-16.5, -1.88) * mm});
            skLineSegment(sketch, "E377.bottom", {"start": v(-13.94, 1.88) * mm, "end": v(-13.23, 1.88) * mm});
            skLineSegment(sketch, "E377.top", {"start": v(-13.94, -1.88) * mm, "end": v(-13.23, -1.88) * mm});
            skLineSegment(sketch, "E377.left", {"start": v(-13.94, 1.88) * mm, "end": v(-13.94, -0.84) * mm});
            skLineSegment(sketch, "E377.right", {"start": v(-13.23, 1.88) * mm, "end": v(-13.23, -1.88) * mm});
            skLineSegment(sketch, "E378", {"start": v(-15.57, 1.88) * mm, "end": v(-13.94, -0.84) * mm});
            skLineSegment(sketch, "E379", {"start": v(-15.8, 0.98) * mm, "end": v(-14.2, -1.88) * mm});
            skLineSegment(sketch, "E380", {"start": v(-14.2, -1.88) * mm, "end": v(-13.94, -1.88) * mm});
            skLineSegment(sketch, "E381", {"start": v(-15.57, 1.88) * mm, "end": v(-15.8, 1.88) * mm});
            skLineSegment(sketch, "E382.trimOffspring", {"start": v(-15.8, 0.98) * mm, "end": v(-15.8, -1.88) * mm});
            skLineSegment(sketch, "E383", {"start": v(29.57, 1.85) * mm, "end": v(29.57, 1.24) * mm});
            skLineSegment(sketch, "E384", {"start": v(29.57, 1.24) * mm, "end": v(30.48, 1.24) * mm});
            skLineSegment(sketch, "E385", {"start": v(30.48, 1.24) * mm, "end": v(30.48, -1.92) * mm});
            skLineSegment(sketch, "E386", {"start": v(30.48, -1.92) * mm, "end": v(31.2, -1.92) * mm});
            skLineSegment(sketch, "E387", {"start": v(31.2, -1.92) * mm, "end": v(31.2, 1.24) * mm});
            skLineSegment(sketch, "E388", {"start": v(31.2, 1.24) * mm, "end": v(32.1, 1.24) * mm});
            skLineSegment(sketch, "E389", {"start": v(32.1, 1.24) * mm, "end": v(32.1, 1.85) * mm});
            skLineSegment(sketch, "E390", {"start": v(32.1, 1.85) * mm, "end": v(29.57, 1.85) * mm});
            skLineSegment(sketch, "E391", {"start": v(35.83, 1.85) * mm, "end": v(35.83, 1.24) * mm});
            skLineSegment(sketch, "E392", {"start": v(35.83, 1.24) * mm, "end": v(36.74, 1.24) * mm});
            skLineSegment(sketch, "E393", {"start": v(36.74, 1.24) * mm, "end": v(36.74, -1.91) * mm});
            skLineSegment(sketch, "E394", {"start": v(36.74, -1.91) * mm, "end": v(37.45, -1.91) * mm});
            skLineSegment(sketch, "E395", {"start": v(37.45, -1.91) * mm, "end": v(37.45, 1.24) * mm});
            skLineSegment(sketch, "E396", {"start": v(37.45, 1.24) * mm, "end": v(38.37, 1.25) * mm});
            skLineSegment(sketch, "E397", {"start": v(38.37, 1.25) * mm, "end": v(38.37, 1.85) * mm});
            skLineSegment(sketch, "E398", {"start": v(38.37, 1.85) * mm, "end": v(35.83, 1.85) * mm});
            skLineSegment(sketch, "E399.bottom", {"start": v(14.69, 1.83) * mm, "end": v(15.4, 1.83) * mm});
            skLineSegment(sketch, "E399.top", {"start": v(14.69, -1.93) * mm, "end": v(15.4, -1.93) * mm});
            skLineSegment(sketch, "E399.left", {"start": v(14.69, 1.83) * mm, "end": v(14.69, -1.93) * mm});
            skLineSegment(sketch, "E399.right", {"start": v(15.4, 1.83) * mm, "end": v(15.4, 1.8) * mm});
            skLineSegment(sketch, "E400.bottom", {"start": v(17.8, 1.83) * mm, "end": v(18.52, 1.83) * mm});
            skLineSegment(sketch, "E400.top", {"start": v(17.8, -1.93) * mm, "end": v(18.52, -1.93) * mm});
            skLineSegment(sketch, "E400.right", {"start": v(18.52, 1.83) * mm, "end": v(18.52, -1.93) * mm});
            skLineSegment(sketch, "E401.left", {"start": v(24.62, -0.37) * mm, "end": v(23.62, -0.37) * mm});
            skLineSegment(sketch, "E401.right", {"start": v(24.85, -1.08) * mm, "end": v(23.4, -1.08) * mm});
            skLineSegment(sketch, "E402", {"start": v(22.3, -1.93) * mm, "end": v(23.63, 1.8) * mm});
            skLineSegment(sketch, "E403", {"start": v(23.13, -1.92) * mm, "end": v(23.4, -1.08) * mm});
            skLineSegment(sketch, "E404.MirrorCS", {"start": v(25.95, -1.92) * mm, "end": v(24.62, 1.8) * mm});
            skLineSegment(sketch, "E405.MirrorCS", {"start": v(25.11, -1.92) * mm, "end": v(24.85, -1.08) * mm});
            skLineSegment(sketch, "E406", {"start": v(23.63, 1.8) * mm, "end": v(24.62, 1.8) * mm});
            skLineSegment(sketch, "E407", {"start": v(22.3, -1.93) * mm, "end": v(23.13, -1.92) * mm});
            skLineSegment(sketch, "E408", {"start": v(25.11, -1.92) * mm, "end": v(25.95, -1.92) * mm});
            skLineSegment(sketch, "E409.trimOffspring", {"start": v(23.62, -0.37) * mm, "end": v(24.12, 1.2) * mm});
            skLineSegment(sketch, "E410.trimOffspring", {"start": v(24.62, -0.37) * mm, "end": v(24.12, 1.2) * mm});
            skLineSegment(sketch, "E411", {"start": v(15.4, 1.83) * mm, "end": v(15.72, 1.83) * mm});
            skLineSegment(sketch, "E412", {"start": v(15.72, 1.83) * mm, "end": v(16.6, -1.08) * mm});
            skLineSegment(sketch, "E413", {"start": v(16.25, -1.93) * mm, "end": v(15.4, 0.99) * mm});
            skLineSegment(sketch, "E414.MirrorCS", {"start": v(17.49, 1.83) * mm, "end": v(16.6, -1.08) * mm});
            skLineSegment(sketch, "E415.MirrorCS", {"start": v(16.97, -1.93) * mm, "end": v(17.8, 0.99) * mm});
            skLineSegment(sketch, "E416", {"start": v(16.25, -1.93) * mm, "end": v(16.97, -1.93) * mm});
            skLineSegment(sketch, "E417.trimOffspring", {"start": v(17.8, 0.99) * mm, "end": v(17.8, -1.93) * mm});
            skLineSegment(sketch, "E418", {"start": v(17.49, 1.83) * mm, "end": v(17.8, 1.83) * mm});
            skLineSegment(sketch, "E419.trimOffspring", {"start": v(15.4, 0.99) * mm, "end": v(15.4, -1.93) * mm});
            skLineSegment(sketch, "E420", {"start": v(-0.74, -0.08) * mm, "end": v(0.85, -1.63) * mm});
            skLineSegment(sketch, "E421", {"start": v(1.9, -2.65) * mm, "end": v(2.33, -2.21) * mm});
            skLineSegment(sketch, "E422", {"start": v(2.33, -2.21) * mm, "end": v(1.68, -1.59) * mm});
            skFitSpline(sketch, "E423", {"points": [v(0.85, -1.63) * mm, v(-0.1, -2.17) * mm, v(-0.9, -2.16) * mm, v(-1.5, -1.74) * mm, v(-1.57, -0.96) * mm, v(-0.74, -0.08) * mm], "startDerivative": vector(-3.96, -3.5) * mm, "endDerivative": vector(4.5, 3.58) * mm});
            skFitSpline(sketch, "E424", {"points": [v(0.85, -1.63) * mm, v(1.25, -1.17) * mm, v(1.8, -0.06) * mm], "startDerivative": vector(1.06, 0.87) * mm, "endDerivative": vector(0.42, 2.27) * mm});
            skLineSegment(sketch, "E425", {"start": v(1.8, -0.06) * mm, "end": v(2.5, -0.06) * mm});
            skFitSpline(sketch, "E426", {"points": [v(-0.74, -0.08) * mm, v(0.4, 0.6) * mm, v(0.95, 1.54) * mm, v(0.66, 2.45) * mm, v(0.16, 2.8) * mm, v(-0.9, 2.8) * mm, v(-1.51, 2.45) * mm, v(-1.78, 1.96) * mm, v(-1.8, 1.34) * mm, v(-1.49, 0.73) * mm, v(-1.14, 0.3) * mm], "startDerivative": vector(9.54, 4.63) * mm, "endDerivative": vector(4.16, -4.73) * mm});
            skLineSegment(sketch, "E427", {"start": v(-0.75, 0.82) * mm, "end": v(-0.56, 0.63) * mm});
            skLineSegment(sketch, "E428", {"start": v(-0.56, 0.63) * mm, "end": v(-0.41, 0.77) * mm});
            skFitSpline(sketch, "E429", {"points": [v(-0.41, 0.77) * mm, v(0.06, 1.18) * mm, v(0.25, 1.6) * mm, v(0.1, 2.05) * mm, v(-0.35, 2.32) * mm, v(-0.74, 2.28) * mm, v(-1.07, 2.03) * mm, v(-1.16, 1.61) * mm, v(-1.02, 1.2) * mm, v(-0.75, 0.82) * mm], "startDerivative": vector(4.08, 3.05) * mm, "endDerivative": vector(2.57, -3.3) * mm});
            skFitSpline(sketch, "E430", {"points": [v(-1.14, 0.3) * mm, v(-2.08, -0.45) * mm, v(-2.3, -1.35) * mm, v(-2.05, -2.24) * mm, v(-1.35, -2.69) * mm, v(-0.52, -2.78) * mm, v(0.28, -2.66) * mm, v(1.05, -2.27) * mm, v(1.3, -2.06) * mm, v(1.68, -1.59) * mm, v(2.5, -0.06) * mm], "startDerivative": vector(-9.37, -5.87) * mm, "endDerivative": vector(3.06, 14.04) * mm});
            skLineSegment(sketch, "E431.trimOffspring", {"start": v(1.25, -1.17) * mm, "end": v(-0.17, 0.2) * mm});
            skLineSegment(sketch, "E432.trimOffspring", {"start": v(1.3, -2.06) * mm, "end": v(1.9, -2.65) * mm});
            skFitSpline(sketch, "E433.trimOffspring", {"points": [v(-1.14, 0.3) * mm, v(-2.08, -0.45) * mm, v(-2.3, -1.35) * mm, v(-2.05, -2.24) * mm, v(-1.35, -2.69) * mm, v(-0.52, -2.78) * mm, v(0.28, -2.66) * mm, v(1.05, -2.27) * mm, v(1.3, -2.06) * mm, v(1.68, -1.59) * mm, v(2.5, -0.06) * mm], "startDerivative": vector(-9.37, -5.87) * mm, "endDerivative": vector(3.06, 14.04) * mm});
            skSolve(sketch);
        }
        {
            var Q0;
            Q0=makeQuery(id+"F1.imprint","IMPRINT",FACE,{"disambiguationData":[TD([[makeQuery(id+"F1.imprint","IMPRINT",EDGE,{"derivedFrom":sQuery(id+"F1.wireOp",EDGE,"E0")}),-1.0]])]});
            extrude(context, id + "F10", {"entities" : qUnion([Q0]), "depth" : 10 * mm, "offsetDistance" : 25 * mm});
        }
        {
            var Q0;
            Q0=makeQuery(id+"F10.opExtrude","CAP_EDGE",EDGE,{"disambiguationData":[OSD([sQuery(id+"F1.wireOp",EDGE,"E1")])],"isStart":false});
            chamfer(context, id + "F11", {"entities" : qUnion([Q0]), "width" : 1 * mm, "tangentPropagation" : true});
        }
        {
            var Q0;
            Q0=makeQuery(id+"F5.imprint","IMPRINT",FACE,{"disambiguationData":[TD([[makeQuery(id+"F5.imprint","IMPRINT",EDGE,{"derivedFrom":sQuery(id+"F5.wireOp",EDGE,"E56")}),-1.0]])]});
            var Q1;
            {var subQ2=sQuery(id+"F5.wireOp",EDGE,"E71");Q1=makeQuery(id+"F5.imprint","IMPRINT",FACE,{"disambiguationData":[TD([[makeQuery(id+"F5.imprint","IMPRINT",EDGE,{"derivedFrom":subQ2}),-1.0]])]});}
            var Q2;
            Q2=makeQuery(id+"F5.imprint","IMPRINT",FACE,{"disambiguationData":[TD([[makeQuery(id+"F5.imprint","IMPRINT",EDGE,{"derivedFrom":sQuery(id+"F5.wireOp",EDGE,"E59")}),1.0]])]});
            var Q3;
            Q3=makeQuery(id+"F5.imprint","IMPRINT",FACE,{"disambiguationData":[TD([[makeQuery(id+"F5.imprint","IMPRINT",EDGE,{"derivedFrom":sQuery(id+"F5.wireOp",EDGE,"E62")}),-1.0]])]});
            var Q4;
            Q4=makeQuery(id+"F5.imprint","IMPRINT",FACE,{"disambiguationData":[TD([[makeQuery(id+"F5.imprint","IMPRINT",EDGE,{"derivedFrom":sQuery(id+"F5.wireOp",EDGE,"E43")}),-1.0]])]});
            var Q5;
            Q5=makeQuery(id+"F5.imprint","IMPRINT",FACE,{"disambiguationData":[TD([[makeQuery(id+"F5.imprint","IMPRINT",EDGE,{"derivedFrom":sQuery(id+"F5.wireOp",EDGE,"E37")}),-1.0]])]});
            var Q6;
            Q6=makeQuery(id+"F5.imprint","IMPRINT",FACE,{"disambiguationData":[TD([[makeQuery(id+"F5.imprint","IMPRINT",EDGE,{"derivedFrom":sQuery(id+"F5.wireOp",EDGE,"E112")}),-1.0]])]});
            var Q7;
            Q7=makeQuery(id+"F5.imprint","IMPRINT",FACE,{"disambiguationData":[TD([[makeQuery(id+"F5.imprint","IMPRINT",EDGE,{"derivedFrom":sQuery(id+"F5.wireOp",EDGE,"E124")}),1.0]])]});
            var Q8;
            Q8=makeQuery(id+"F5.imprint","IMPRINT",FACE,{"disambiguationData":[TD([[makeQuery(id+"F5.imprint","IMPRINT",EDGE,{"derivedFrom":sQuery(id+"F5.wireOp",EDGE,"E161")}),1.0]])]});
            var Q9;
            Q9=makeQuery(id+"F5.imprint","IMPRINT",FACE,{"disambiguationData":[TD([[makeQuery(id+"F5.imprint","IMPRINT",EDGE,{"derivedFrom":sQuery(id+"F5.wireOp",EDGE,"E137")}),1.0]])]});
            extrude(context, id + "F12", {"entities" : qUnion([Q0, Q1, Q2, Q3, Q4, Q5, Q6, Q7, Q8, Q9]), "depth" : 1 * mm, "offsetDistance" : 25 * mm});
        }
        {
            var Q0;
            Q0 = qSketchRegion(id + "F6", true);
            extrude(context, id + "F13", {"entities" : qUnion([Q0]), "depth" : 1 * mm, "offsetDistance" : 25 * mm});
        }
        {
            var Q0;
            Q0 = qSketchRegion(id + "F7", true);
            var Q1;
            {var subQ0=sQuery(id+"F7.wireOp",EDGE,"E325.1");var subQ1=sQuery(id+"F7.wireOp",EDGE,"b35f8b2a-4b94-4131-818a-57236e89b0ba");var subQ2=makeQuery(id+"F7.imprint","INTERSECT",VERTEX,{"disambiguationData":[OD(1.0)],"derivedFrom":[subQ1,subQ0]});Q1=makeQuery(id+"F7.imprint","IMPRINT",FACE,{"disambiguationData":[TD([[makeQuery(id+"F7.imprint","IMPRINT",EDGE,{"disambiguationData":[TD([[subQ2,-1.0]])],"derivedFrom":subQ1}),1.0]])]});}
            var Q2;
            {var subQ0=sQuery(id+"F7.wireOp",EDGE,"E325.1");var subQ1=sQuery(id+"F7.wireOp",EDGE,"b35f8b2a-4b94-4131-818a-57236e89b0ba");var subQ2=makeQuery(id+"F7.imprint","INTERSECT",VERTEX,{"disambiguationData":[OD(0.0)],"derivedFrom":[subQ1,subQ0]});Q2=makeQuery(id+"F7.imprint","IMPRINT",FACE,{"disambiguationData":[TD([[makeQuery(id+"F7.imprint","IMPRINT",EDGE,{"disambiguationData":[TD([[subQ2,1.0]])],"derivedFrom":subQ1}),1.0]])]});}
            extrude(context, id + "F14", {"entities" : qUnion([Q0, Q1, Q2]), "depth" : 12 * mm, "offsetDistance" : 25 * mm});
        }
        {
            var Q0;
            Q0=makeQuery(id+"F7.imprint","IMPRINT",FACE,{"disambiguationData":[TD([[makeQuery(id+"F7.imprint","IMPRINT",EDGE,{"derivedFrom":sQuery(id+"F7.wireOp",EDGE,"E324.0")}),-1.0]])]});
            extrude(context, id + "F15", {"entities" : qUnion([Q0]), "depth" : 11 * mm, "offsetDistance" : 25 * mm, "hasSecondDirection" : true, "secondDirectionOppositeDirection" : false, "secondDirectionDepth" : 1 * mm});
        }
        {
            var Q0;
            Q0=makeQuery(id+"F8.imprint","IMPRINT",FACE,{"disambiguationData":[TD([[makeQuery(id+"F8.imprint","IMPRINT",EDGE,{"derivedFrom":sQuery(id+"F8.wireOp",EDGE,"E326")}),1.0]])]});
            var Q1;
            Q1=makeQuery(id+"F8.imprint","IMPRINT",FACE,{"disambiguationData":[TD([[makeQuery(id+"F8.imprint","IMPRINT",EDGE,{"derivedFrom":sQuery(id+"F8.wireOp",EDGE,"E337.0")}),1.0]])]});
            extrude(context, id + "F16", {"entities" : qUnion([Q0, Q1]), "depth" : 12.1 * mm, "offsetDistance" : 25 * mm, "hasSecondDirection" : true, "secondDirectionOppositeDirection" : false, "secondDirectionDepth" : 1 * mm});
        }
        {
            var Q0;
            Q0=makeQuery(id+"F8.imprint","IMPRINT",FACE,{"disambiguationData":[TD([[makeQuery(id+"F8.imprint","IMPRINT",EDGE,{"derivedFrom":sQuery(id+"F8.wireOp",EDGE,"E326")}),-1.0]])]});
            var Q1;
            Q1=makeQuery(id+"F8.imprint","IMPRINT",FACE,{"disambiguationData":[TD([[makeQuery(id+"F8.imprint","IMPRINT",EDGE,{"derivedFrom":sQuery(id+"F8.wireOp",EDGE,"E336")}),1.0]])]});
            extrude(context, id + "F17", {"entities" : qUnion([Q0, Q1]), "depth" : 13 * mm, "offsetDistance" : 25 * mm});
        }
        {
            var Q0;
            Q0 = qSketchRegion(id + "F3", true);
            var Q1;
            Q1=makeQuery(id+"F10.opExtrude","CAP_FACE",FACE,{"disambiguationData":[OSD([sQuery(id+"F1.wireOp",EDGE,"E0"),sQuery(id+"F1.wireOp",EDGE,"E1")])],"isStart":true});
            extrude(context, id + "F18", {"entities" : qUnion([Q0, Q1]), "operationType" : NewBodyOperationType.REMOVE, "depth" : 1.11 * mm, "offsetDistance" : 25 * mm});
        }
        {
            var Q0;
            {var subQ0=sQuery(id+"F2.wireOp",EDGE,"E34.trimOffspring");Q0=makeQuery(id+"F2.imprint","IMPRINT",FACE,{"disambiguationData":[TD([[makeQuery(id+"F2.imprint","IMPRINT",EDGE,{"derivedFrom":subQ0}),1.0]])]});}
            var Q1;
            Q1=makeQuery(id+"F2.imprint","IMPRINT",FACE,{"disambiguationData":[TD([[makeQuery(id+"F2.imprint","IMPRINT",EDGE,{"derivedFrom":sQuery(id+"F2.wireOp",EDGE,"E3.0")}),1.0]])]});
            var Q2;
            {var subQ0=sQuery(id+"F2.wireOp",EDGE,"E32.trimOffspring");Q2=makeQuery(id+"F2.imprint","IMPRINT",FACE,{"disambiguationData":[TD([[makeQuery(id+"F2.imprint","IMPRINT",EDGE,{"derivedFrom":subQ0}),1.0]])]});}
            var Q3;
            {var subQ0=sQuery(id+"F2.wireOp",EDGE,"E30.trimOffspring");Q3=makeQuery(id+"F2.imprint","IMPRINT",FACE,{"disambiguationData":[TD([[makeQuery(id+"F2.imprint","IMPRINT",EDGE,{"derivedFrom":subQ0}),1.0]])]});}
            var Q4;
            {var subQ0=sQuery(id+"F2.wireOp",EDGE,"E28.trimOffspring");Q4=makeQuery(id+"F2.imprint","IMPRINT",FACE,{"disambiguationData":[TD([[makeQuery(id+"F2.imprint","IMPRINT",EDGE,{"derivedFrom":subQ0}),1.0]])]});}
            var Q5;
            {var subQ0=sQuery(id+"F2.wireOp",EDGE,"E26.trimOffspring");Q5=makeQuery(id+"F2.imprint","IMPRINT",FACE,{"disambiguationData":[TD([[makeQuery(id+"F2.imprint","IMPRINT",EDGE,{"derivedFrom":subQ0}),1.0]])]});}
            var Q6;
            {var subQ0=sQuery(id+"F2.wireOp",EDGE,"E24.trimOffspring");Q6=makeQuery(id+"F2.imprint","IMPRINT",FACE,{"disambiguationData":[TD([[makeQuery(id+"F2.imprint","IMPRINT",EDGE,{"derivedFrom":subQ0}),1.0]])]});}
            var Q7;
            {var subQ0=sQuery(id+"F2.wireOp",EDGE,"E22.trimOffspring");Q7=makeQuery(id+"F2.imprint","IMPRINT",FACE,{"disambiguationData":[TD([[makeQuery(id+"F2.imprint","IMPRINT",EDGE,{"derivedFrom":subQ0}),1.0]])]});}
            var Q8;
            {var subQ0=sQuery(id+"F2.wireOp",EDGE,"E7.0.2.0");Q8=makeQuery(id+"F2.imprint","IMPRINT",FACE,{"disambiguationData":[TD([[makeQuery(id+"F2.imprint","IMPRINT",EDGE,{"derivedFrom":subQ0}),1.0]])]});}
            var Q9;
            {var subQ0=sQuery(id+"F2.wireOp",EDGE,"E7.0.1.0");Q9=makeQuery(id+"F2.imprint","IMPRINT",FACE,{"disambiguationData":[TD([[makeQuery(id+"F2.imprint","IMPRINT",EDGE,{"derivedFrom":subQ0}),1.0]])]});}
            var Q10;
            {var subQ0=sQuery(id+"F2.wireOp",EDGE,"E5");Q10=makeQuery(id+"F2.imprint","IMPRINT",FACE,{"disambiguationData":[TD([[makeQuery(id+"F2.imprint","IMPRINT",EDGE,{"derivedFrom":subQ0}),1.0]])]});}
            var Q11;
            {var subQ0=sQuery(id+"F2.wireOp",EDGE,"E6");Q11=makeQuery(id+"F2.imprint","IMPRINT",FACE,{"disambiguationData":[TD([[makeQuery(id+"F2.imprint","IMPRINT",EDGE,{"derivedFrom":subQ0}),-1.0]])]});}
            var Q12;
            {var subQ0=sQuery(id+"F2.wireOp",EDGE,"E7.1.8.0");Q12=makeQuery(id+"F2.imprint","IMPRINT",FACE,{"disambiguationData":[TD([[makeQuery(id+"F2.imprint","IMPRINT",EDGE,{"derivedFrom":subQ0}),1.0]])]});}
            var Q13;
            {var subQ0=sQuery(id+"F2.wireOp",EDGE,"E7.1.7.0");Q13=makeQuery(id+"F2.imprint","IMPRINT",FACE,{"disambiguationData":[TD([[makeQuery(id+"F2.imprint","IMPRINT",EDGE,{"derivedFrom":subQ0}),1.0]])]});}
            var Q14;
            {var subQ0=sQuery(id+"F2.wireOp",EDGE,"E7.1.7.1");Q14=makeQuery(id+"F2.imprint","IMPRINT",FACE,{"disambiguationData":[TD([[makeQuery(id+"F2.imprint","IMPRINT",EDGE,{"derivedFrom":subQ0}),-1.0]])]});}
            var Q15;
            {var subQ0=sQuery(id+"F2.wireOp",EDGE,"E17.trimOffspring");Q15=makeQuery(id+"F2.imprint","IMPRINT",FACE,{"disambiguationData":[TD([[makeQuery(id+"F2.imprint","IMPRINT",EDGE,{"derivedFrom":subQ0}),1.0]])]});}
            var Q16;
            {var subQ0=sQuery(id+"F2.wireOp",EDGE,"E14.trimOffspring");Q16=makeQuery(id+"F2.imprint","IMPRINT",FACE,{"disambiguationData":[TD([[makeQuery(id+"F2.imprint","IMPRINT",EDGE,{"derivedFrom":subQ0}),1.0]])]});}
            var Q17;
            {var subQ0=sQuery(id+"F2.wireOp",EDGE,"E13.trimOffspring");Q17=makeQuery(id+"F2.imprint","IMPRINT",FACE,{"disambiguationData":[TD([[makeQuery(id+"F2.imprint","IMPRINT",EDGE,{"derivedFrom":subQ0}),1.0]])]});}
            var Q18;
            {var subQ0=sQuery(id+"F2.wireOp",EDGE,"E11.trimOffspring");Q18=makeQuery(id+"F2.imprint","IMPRINT",FACE,{"disambiguationData":[TD([[makeQuery(id+"F2.imprint","IMPRINT",EDGE,{"derivedFrom":subQ0}),1.0]])]});}
            var Q19;
            {var subQ0=sQuery(id+"F2.wireOp",EDGE,"E9.trimOffspring");Q19=makeQuery(id+"F2.imprint","IMPRINT",FACE,{"disambiguationData":[TD([[makeQuery(id+"F2.imprint","IMPRINT",EDGE,{"derivedFrom":subQ0}),1.0]])]});}
            var Q20;
            {var subQ0=sQuery(id+"F2.wireOp",EDGE,"E8.trimOffspring");Q20=makeQuery(id+"F2.imprint","IMPRINT",FACE,{"disambiguationData":[TD([[makeQuery(id+"F2.imprint","IMPRINT",EDGE,{"derivedFrom":subQ0}),-1.0]])]});}
            extrude(context, id + "F19", {"entities" : qUnion([Q0, Q1, Q2, Q3, Q4, Q5, Q6, Q7, Q8, Q9, Q10, Q11, Q12, Q13, Q14, Q15, Q16, Q17, Q18, Q19, Q20]), "depth" : 9 * mm, "offsetDistance" : 25 * mm});
        }
        {
            var Q0;
            Q0=makeQuery(id+"F2.imprint","IMPRINT",FACE,{"disambiguationData":[TD([[makeQuery(id+"F2.imprint","IMPRINT",EDGE,{"derivedFrom":sQuery(id+"F2.wireOp",EDGE,"E2")}),1.0]])]});
            var Q1;
            {var subQ0=sQuery(id+"F2.wireOp",EDGE,"E33.trimOffspring");Q1=makeQuery(id+"F2.imprint","IMPRINT",FACE,{"disambiguationData":[TD([[makeQuery(id+"F2.imprint","IMPRINT",EDGE,{"derivedFrom":subQ0}),1.0]])]});}
            var Q2;
            {var subQ0=sQuery(id+"F2.wireOp",EDGE,"E31.trimOffspring");Q2=makeQuery(id+"F2.imprint","IMPRINT",FACE,{"disambiguationData":[TD([[makeQuery(id+"F2.imprint","IMPRINT",EDGE,{"derivedFrom":subQ0}),1.0]])]});}
            var Q3;
            {var subQ0=sQuery(id+"F2.wireOp",EDGE,"E29.trimOffspring");Q3=makeQuery(id+"F2.imprint","IMPRINT",FACE,{"disambiguationData":[TD([[makeQuery(id+"F2.imprint","IMPRINT",EDGE,{"derivedFrom":subQ0}),1.0]])]});}
            var Q4;
            {var subQ0=sQuery(id+"F2.wireOp",EDGE,"E27.trimOffspring");Q4=makeQuery(id+"F2.imprint","IMPRINT",FACE,{"disambiguationData":[TD([[makeQuery(id+"F2.imprint","IMPRINT",EDGE,{"derivedFrom":subQ0}),1.0]])]});}
            var Q5;
            {var subQ0=sQuery(id+"F2.wireOp",EDGE,"E25.trimOffspring");Q5=makeQuery(id+"F2.imprint","IMPRINT",FACE,{"disambiguationData":[TD([[makeQuery(id+"F2.imprint","IMPRINT",EDGE,{"derivedFrom":subQ0}),1.0]])]});}
            var Q6;
            {var subQ0=sQuery(id+"F2.wireOp",EDGE,"E23.trimOffspring");Q6=makeQuery(id+"F2.imprint","IMPRINT",FACE,{"disambiguationData":[TD([[makeQuery(id+"F2.imprint","IMPRINT",EDGE,{"derivedFrom":subQ0}),1.0]])]});}
            var Q7;
            {var subQ0=sQuery(id+"F2.wireOp",EDGE,"E21.trimOffspring");Q7=makeQuery(id+"F2.imprint","IMPRINT",FACE,{"disambiguationData":[TD([[makeQuery(id+"F2.imprint","IMPRINT",EDGE,{"derivedFrom":subQ0}),1.0]])]});}
            var Q8;
            {var subQ0=sQuery(id+"F2.wireOp",EDGE,"E7.0.2.0");Q8=makeQuery(id+"F2.imprint","IMPRINT",FACE,{"disambiguationData":[TD([[makeQuery(id+"F2.imprint","IMPRINT",EDGE,{"derivedFrom":subQ0}),-1.0]])]});}
            var Q9;
            {var subQ0=sQuery(id+"F2.wireOp",EDGE,"E7.0.1.0");Q9=makeQuery(id+"F2.imprint","IMPRINT",FACE,{"disambiguationData":[TD([[makeQuery(id+"F2.imprint","IMPRINT",EDGE,{"derivedFrom":subQ0}),-1.0]])]});}
            var Q10;
            {var subQ0=sQuery(id+"F2.wireOp",EDGE,"E5");Q10=makeQuery(id+"F2.imprint","IMPRINT",FACE,{"disambiguationData":[TD([[makeQuery(id+"F2.imprint","IMPRINT",EDGE,{"derivedFrom":subQ0}),-1.0]])]});}
            var Q11;
            {var subQ0=sQuery(id+"F2.wireOp",EDGE,"E7.1.9.0");Q11=makeQuery(id+"F2.imprint","IMPRINT",FACE,{"disambiguationData":[TD([[makeQuery(id+"F2.imprint","IMPRINT",EDGE,{"derivedFrom":subQ0}),-1.0]])]});}
            var Q12;
            {var subQ0=sQuery(id+"F2.wireOp",EDGE,"E7.1.8.0");Q12=makeQuery(id+"F2.imprint","IMPRINT",FACE,{"disambiguationData":[TD([[makeQuery(id+"F2.imprint","IMPRINT",EDGE,{"derivedFrom":subQ0}),-1.0]])]});}
            var Q13;
            {var subQ0=sQuery(id+"F2.wireOp",EDGE,"E7.1.7.0");Q13=makeQuery(id+"F2.imprint","IMPRINT",FACE,{"disambiguationData":[TD([[makeQuery(id+"F2.imprint","IMPRINT",EDGE,{"derivedFrom":subQ0}),-1.0]])]});}
            var Q14;
            {var subQ0=sQuery(id+"F2.wireOp",EDGE,"E18.trimOffspring");Q14=makeQuery(id+"F2.imprint","IMPRINT",FACE,{"disambiguationData":[TD([[makeQuery(id+"F2.imprint","IMPRINT",EDGE,{"derivedFrom":subQ0}),1.0]])]});}
            var Q15;
            {var subQ0=sQuery(id+"F2.wireOp",EDGE,"E16.trimOffspring");Q15=makeQuery(id+"F2.imprint","IMPRINT",FACE,{"disambiguationData":[TD([[makeQuery(id+"F2.imprint","IMPRINT",EDGE,{"derivedFrom":subQ0}),1.0]])]});}
            var Q16;
            {var subQ0=sQuery(id+"F2.wireOp",EDGE,"E14.trimOffspring");Q16=makeQuery(id+"F2.imprint","IMPRINT",FACE,{"disambiguationData":[TD([[makeQuery(id+"F2.imprint","IMPRINT",EDGE,{"derivedFrom":subQ0}),-1.0]])]});}
            var Q17;
            {var subQ0=sQuery(id+"F2.wireOp",EDGE,"E12.trimOffspring");Q17=makeQuery(id+"F2.imprint","IMPRINT",FACE,{"disambiguationData":[TD([[makeQuery(id+"F2.imprint","IMPRINT",EDGE,{"derivedFrom":subQ0}),1.0]])]});}
            var Q18;
            {var subQ0=sQuery(id+"F2.wireOp",EDGE,"E10.trimOffspring");Q18=makeQuery(id+"F2.imprint","IMPRINT",FACE,{"disambiguationData":[TD([[makeQuery(id+"F2.imprint","IMPRINT",EDGE,{"derivedFrom":subQ0}),1.0]])]});}
            var Q19;
            {var subQ0=sQuery(id+"F2.wireOp",EDGE,"E8.trimOffspring");Q19=makeQuery(id+"F2.imprint","IMPRINT",FACE,{"disambiguationData":[TD([[makeQuery(id+"F2.imprint","IMPRINT",EDGE,{"derivedFrom":subQ0}),1.0]])]});}
            extrude(context, id + "F20", {"entities" : qUnion([Q0, Q1, Q2, Q3, Q4, Q5, Q6, Q7, Q8, Q9, Q10, Q11, Q12, Q13, Q14, Q15, Q16, Q17, Q18, Q19]), "depth" : 8 * mm, "offsetDistance" : 25 * mm, "hasSecondDirection" : true, "secondDirectionOppositeDirection" : false, "secondDirectionDepth" : 1 * mm});
        }
        {
            var Q0;
            Q0=makeQuery(id+"F9.imprint","IMPRINT",FACE,{"disambiguationData":[TD([[makeQuery(id+"F9.imprint","IMPRINT",EDGE,{"derivedFrom":sQuery(id+"F9.wireOp",EDGE,"E420")}),1.0]])]});
            extrude(context, id + "F21", {"entities" : qUnion([Q0]), "depth" : 2 * mm, "offsetDistance" : 25 * mm});
        }
        {
            var Q0;
            Q0=makeQuery(id+"F9.imprint","IMPRINT",FACE,{"disambiguationData":[TD([[makeQuery(id+"F9.imprint","IMPRINT",EDGE,{"derivedFrom":sQuery(id+"F9.wireOp",EDGE,"E399.bottom")}),-1.0]])]});
            var Q1;
            Q1=makeQuery(id+"F9.imprint","IMPRINT",FACE,{"disambiguationData":[TD([[makeQuery(id+"F9.imprint","IMPRINT",EDGE,{"derivedFrom":sQuery(id+"F9.wireOp",EDGE,"E401.left")}),1.0]])]});
            var Q2;
            Q2=makeQuery(id+"F9.imprint","IMPRINT",FACE,{"disambiguationData":[TD([[makeQuery(id+"F9.imprint","IMPRINT",EDGE,{"derivedFrom":sQuery(id+"F9.wireOp",EDGE,"E383")}),1.0]])]});
            var Q3;
            Q3=makeQuery(id+"F9.imprint","IMPRINT",FACE,{"disambiguationData":[TD([[makeQuery(id+"F9.imprint","IMPRINT",EDGE,{"derivedFrom":sQuery(id+"F9.wireOp",EDGE,"E391")}),1.0]])]});
            var Q4;
            Q4=makeQuery(id+"F9.imprint","IMPRINT",FACE,{"disambiguationData":[TD([[makeQuery(id+"F9.imprint","IMPRINT",EDGE,{"derivedFrom":sQuery(id+"F9.wireOp",EDGE,"E376.bottom")}),-1.0]])]});
            var Q5;
            Q5=makeQuery(id+"F9.imprint","IMPRINT",FACE,{"disambiguationData":[TD([[makeQuery(id+"F9.imprint","IMPRINT",EDGE,{"derivedFrom":sQuery(id+"F9.wireOp",EDGE,"E375.bottom")}),-1.0]])]});
            var Q6;
            Q6=makeQuery(id+"F9.imprint","IMPRINT",FACE,{"disambiguationData":[TD([[makeQuery(id+"F9.imprint","IMPRINT",EDGE,{"derivedFrom":sQuery(id+"F9.wireOp",EDGE,"E367")}),1.0]])]});
            var Q7;
            Q7=makeQuery(id+"F9.imprint","IMPRINT",FACE,{"disambiguationData":[TD([[makeQuery(id+"F9.imprint","IMPRINT",EDGE,{"derivedFrom":sQuery(id+"F9.wireOp",EDGE,"E363")}),-1.0]])]});
            var Q8;
            Q8=makeQuery(id+"F9.imprint","IMPRINT",FACE,{"disambiguationData":[TD([[makeQuery(id+"F9.imprint","IMPRINT",EDGE,{"derivedFrom":sQuery(id+"F9.wireOp",EDGE,"E348")}),1.0]])]});
            var Q9;
            Q9=makeQuery(id+"F9.imprint","IMPRINT",FACE,{"disambiguationData":[TD([[makeQuery(id+"F9.imprint","IMPRINT",EDGE,{"derivedFrom":sQuery(id+"F9.wireOp",EDGE,"E345.bottom")}),-1.0]])]});
            extrude(context, id + "F22", {"entities" : qUnion([Q0, Q1, Q2, Q3, Q4, Q5, Q6, Q7, Q8, Q9]), "depth" : 1 * mm, "offsetDistance" : 25 * mm});
        }
    });
